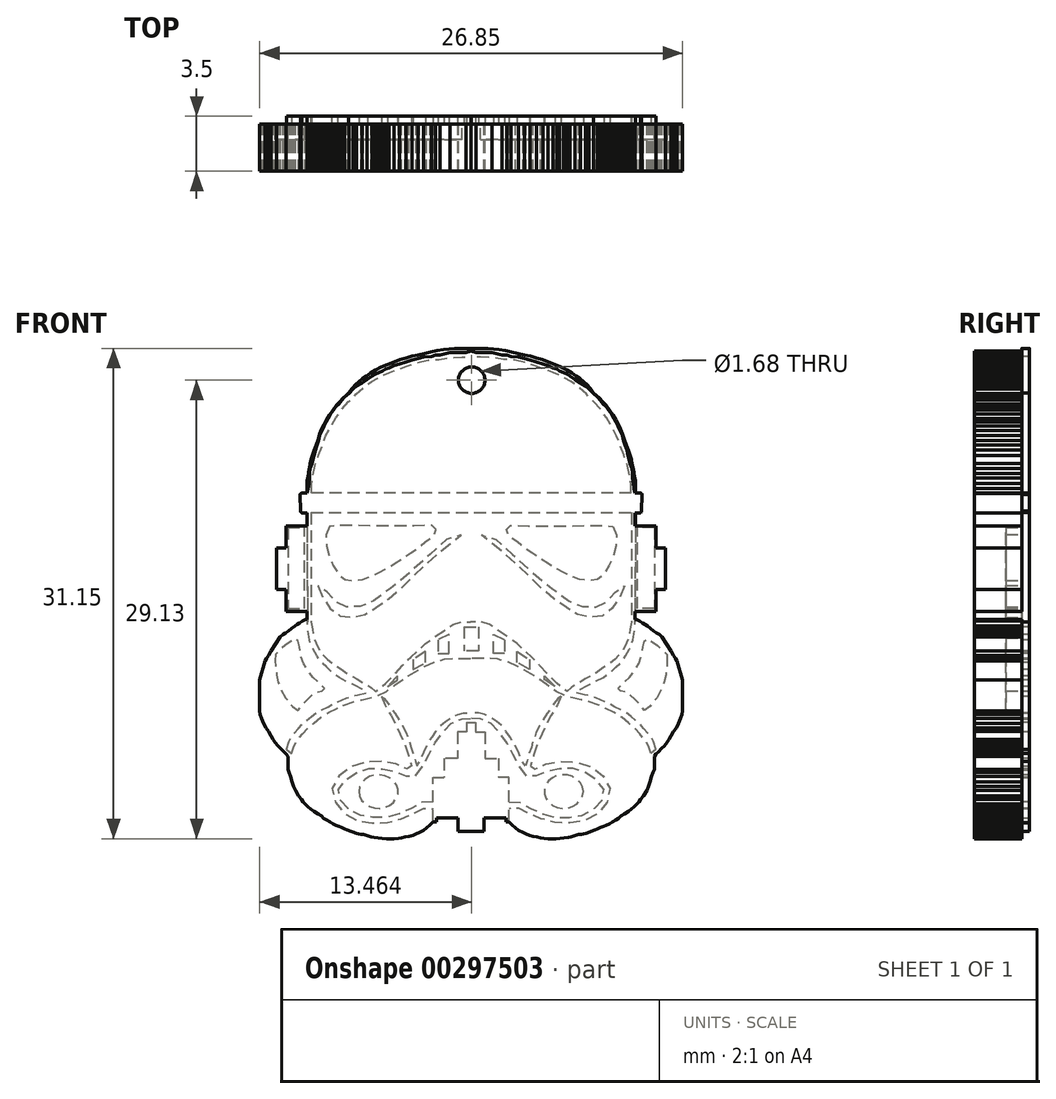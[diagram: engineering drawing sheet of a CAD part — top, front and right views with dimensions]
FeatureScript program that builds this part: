
annotation { "Feature Type Name" : "Feature", "Feature Type Description" : "" }
export const myFeature = defineFeature(function(context is Context, id is Id, definition is map)
    precondition{}
    {
        {
            var Q0;
            Q0=qCreatedBy(makeId("Front.planeOp"),FACE);
            var sketch = newSketch(context, id + "F0", { "sketchPlane" : qUnion([Q0])});
            skLineSegment(sketch, "E0", {"start": v(-15.39, -14.48) * mm, "end": v(-15.53, -14.36) * mm});
            skLineSegment(sketch, "E1", {"start": v(-15.53, -14.36) * mm, "end": v(-15.74, -14.15) * mm});
            skLineSegment(sketch, "E2", {"start": v(-15.74, -14.15) * mm, "end": v(-15.92, -13.98) * mm});
            skLineSegment(sketch, "E3", {"start": v(-15.92, -13.98) * mm, "end": v(-16.08, -13.76) * mm});
            skLineSegment(sketch, "E4", {"start": v(-16.08, -13.76) * mm, "end": v(-16.22, -13.57) * mm});
            skLineSegment(sketch, "E5", {"start": v(-16.22, -13.57) * mm, "end": v(-16.35, -13.35) * mm});
            skLineSegment(sketch, "E6", {"start": v(-16.35, -13.35) * mm, "end": v(-16.5, -13.07) * mm});
            skLineSegment(sketch, "E7", {"start": v(-16.5, -13.07) * mm, "end": v(-16.68, -12.84) * mm});
            skLineSegment(sketch, "E8", {"start": v(-16.68, -12.84) * mm, "end": v(-16.81, -12.57) * mm});
            skLineSegment(sketch, "E9", {"start": v(-16.81, -12.57) * mm, "end": v(-16.95, -12.25) * mm});
            skLineSegment(sketch, "E10", {"start": v(-16.95, -12.25) * mm, "end": v(-17.04, -12) * mm});
            skLineSegment(sketch, "E11", {"start": v(-17.04, -12) * mm, "end": v(-17.07, -11.77) * mm});
            skLineSegment(sketch, "E12", {"start": v(-17.07, -11.77) * mm, "end": v(-17.07, -11.5) * mm});
            skLineSegment(sketch, "E13", {"start": v(-17.07, -11.5) * mm, "end": v(-17.07, -11.27) * mm});
            skLineSegment(sketch, "E14", {"start": v(-17.07, -11.27) * mm, "end": v(-17.07, -10.11) * mm});
            skLineSegment(sketch, "E15", {"start": v(-17.07, -10.11) * mm, "end": v(-17.07, -9.78) * mm});
            skPoint(sketch, "E15.endSnap0", {"position": v(-17.07, -10.7) * mm});
            skLineSegment(sketch, "E16", {"start": v(-17.07, -9.78) * mm, "end": v(-16.99, -9.5) * mm});
            skLineSegment(sketch, "E17", {"start": v(-16.99, -9.5) * mm, "end": v(-16.91, -9.23) * mm});
            skLineSegment(sketch, "E18", {"start": v(-16.91, -9.23) * mm, "end": v(-16.85, -9) * mm});
            skLineSegment(sketch, "E19", {"start": v(-16.85, -9) * mm, "end": v(-16.79, -8.79) * mm});
            skLineSegment(sketch, "E20", {"start": v(-16.79, -8.79) * mm, "end": v(-16.73, -8.58) * mm});
            skLineSegment(sketch, "E21", {"start": v(-16.73, -8.58) * mm, "end": v(-16.63, -8.42) * mm});
            skLineSegment(sketch, "E22", {"start": v(-16.63, -8.42) * mm, "end": v(-16.5, -8.23) * mm});
            skLineSegment(sketch, "E23", {"start": v(-16.5, -8.23) * mm, "end": v(-16.35, -7.95) * mm});
            skLineSegment(sketch, "E24", {"start": v(-16.35, -7.95) * mm, "end": v(-16.14, -7.63) * mm});
            skLineSegment(sketch, "E25", {"start": v(-16.14, -7.63) * mm, "end": v(-15.92, -7.29) * mm});
            skLineSegment(sketch, "E26", {"start": v(-15.92, -7.29) * mm, "end": v(-15.77, -7.05) * mm});
            skLineSegment(sketch, "E27", {"start": v(-15.77, -7.05) * mm, "end": v(-15.6, -6.9) * mm});
            skLineSegment(sketch, "E28", {"start": v(-15.6, -6.9) * mm, "end": v(-15.43, -6.81) * mm});
            skLineSegment(sketch, "E29", {"start": v(-15.43, -6.81) * mm, "end": v(-15.23, -6.67) * mm});
            skLineSegment(sketch, "E30", {"start": v(-15.23, -6.67) * mm, "end": v(-15.04, -6.53) * mm});
            skLineSegment(sketch, "E31", {"start": v(-15.04, -6.53) * mm, "end": v(-14.84, -6.38) * mm});
            skLineSegment(sketch, "E32", {"start": v(-14.84, -6.38) * mm, "end": v(-14.7, -6.28) * mm});
            skLineSegment(sketch, "E33", {"start": v(-14.7, -6.28) * mm, "end": v(-14.54, -6.18) * mm});
            skLineSegment(sketch, "E34", {"start": v(-14.54, -6.18) * mm, "end": v(-14.34, -6.05) * mm});
            skLineSegment(sketch, "E35", {"start": v(-14.34, -6.05) * mm, "end": v(-14.15, -5.96) * mm});
            skLineSegment(sketch, "E36", {"start": v(-14.15, -5.96) * mm, "end": v(-14.06, -5.96) * mm});
            skLineSegment(sketch, "E37", {"start": v(-14.15, 0.83) * mm, "end": v(-14.36, 0.82) * mm});
            skLineSegment(sketch, "E38", {"start": v(-14.48, 0.94) * mm, "end": v(-14.5, 2) * mm});
            skArc(sketch, "E39", {"start": v(-14.48, 0.94) * mm, "mid": v(-14.45, 0.86) * mm, "end": v(-14.36, 0.82) * mm});
            skLineSegment(sketch, "E40", {"start": v(-15.39, -14.48) * mm, "end": v(-15.28, -14.64) * mm});
            skLineSegment(sketch, "E41", {"start": v(-15.28, -14.64) * mm, "end": v(-15.28, -15.48) * mm});
            skLineSegment(sketch, "E42", {"start": v(-15.28, -15.48) * mm, "end": v(-15.2, -15.66) * mm});
            skLineSegment(sketch, "E43", {"start": v(-15.2, -15.66) * mm, "end": v(-15.11, -15.93) * mm});
            skLineSegment(sketch, "E44", {"start": v(-15.11, -15.93) * mm, "end": v(-15, -16.28) * mm});
            skLineSegment(sketch, "E45", {"start": v(-15, -16.28) * mm, "end": v(-14.92, -16.54) * mm});
            skLineSegment(sketch, "E46", {"start": v(-14.92, -16.54) * mm, "end": v(-14.8, -16.82) * mm});
            skLineSegment(sketch, "E47", {"start": v(-14.8, -16.82) * mm, "end": v(-14.6, -17.14) * mm});
            skLineSegment(sketch, "E48", {"start": v(-14.6, -17.14) * mm, "end": v(-14.42, -17.39) * mm});
            skLineSegment(sketch, "E49", {"start": v(-14.42, -17.39) * mm, "end": v(-14.3, -17.52) * mm});
            skLineSegment(sketch, "E50", {"start": v(-14.3, -17.52) * mm, "end": v(-14.18, -17.68) * mm});
            skLineSegment(sketch, "E51", {"start": v(-14.18, -17.68) * mm, "end": v(-14, -17.86) * mm});
            skLineSegment(sketch, "E52", {"start": v(-14, -17.86) * mm, "end": v(-13.84, -18) * mm});
            skLineSegment(sketch, "E53", {"start": v(-13.84, -18) * mm, "end": v(-13.63, -18.15) * mm});
            skLineSegment(sketch, "E54", {"start": v(-13.63, -18.15) * mm, "end": v(-13.38, -18.3) * mm});
            skLineSegment(sketch, "E55", {"start": v(-13.38, -18.3) * mm, "end": v(-13.16, -18.44) * mm});
            skLineSegment(sketch, "E56", {"start": v(-13.16, -18.44) * mm, "end": v(-13, -18.57) * mm});
            skLineSegment(sketch, "E57", {"start": v(-13, -18.57) * mm, "end": v(-12.84, -18.67) * mm});
            skLineSegment(sketch, "E58", {"start": v(-12.84, -18.67) * mm, "end": v(-12.61, -18.81) * mm});
            skLineSegment(sketch, "E59", {"start": v(-12.61, -18.81) * mm, "end": v(-12.42, -18.93) * mm});
            skLineSegment(sketch, "E60", {"start": v(-12.42, -18.93) * mm, "end": v(-12.23, -19.02) * mm});
            skLineSegment(sketch, "E61", {"start": v(-12.23, -19.02) * mm, "end": v(-12.04, -19.09) * mm});
            skLineSegment(sketch, "E62", {"start": v(-12.04, -19.09) * mm, "end": v(-11.86, -19.16) * mm});
            skLineSegment(sketch, "E63", {"start": v(-11.86, -19.16) * mm, "end": v(-11.69, -19.24) * mm});
            skLineSegment(sketch, "E64", {"start": v(-11.69, -19.24) * mm, "end": v(-11.51, -19.31) * mm});
            skLineSegment(sketch, "E65", {"start": v(-11.51, -19.31) * mm, "end": v(-11.34, -19.38) * mm});
            skLineSegment(sketch, "E66", {"start": v(-11.34, -19.38) * mm, "end": v(-11.14, -19.46) * mm});
            skLineSegment(sketch, "E67", {"start": v(-11.14, -19.46) * mm, "end": v(-10.94, -19.53) * mm});
            skLineSegment(sketch, "E68", {"start": v(-10.94, -19.53) * mm, "end": v(-10.8, -19.56) * mm});
            skLineSegment(sketch, "E69", {"start": v(-10.8, -19.56) * mm, "end": v(-10.65, -19.59) * mm});
            skLineSegment(sketch, "E70", {"start": v(-10.65, -19.59) * mm, "end": v(-10.46, -19.59) * mm});
            skLineSegment(sketch, "E71", {"start": v(-10.46, -19.59) * mm, "end": v(-10.23, -19.68) * mm});
            skLineSegment(sketch, "E72", {"start": v(-10.23, -19.68) * mm, "end": v(-10, -19.76) * mm});
            skLineSegment(sketch, "E73", {"start": v(-10, -19.76) * mm, "end": v(-9.82, -19.79) * mm});
            skLineSegment(sketch, "E74", {"start": v(-9.82, -19.79) * mm, "end": v(-9.55, -19.82) * mm});
            skLineSegment(sketch, "E75", {"start": v(-9.55, -19.82) * mm, "end": v(-9.3, -19.85) * mm});
            skLineSegment(sketch, "E76", {"start": v(-9.3, -19.85) * mm, "end": v(-9.03, -19.88) * mm});
            skLineSegment(sketch, "E77", {"start": v(-9.03, -19.88) * mm, "end": v(-8.8, -19.88) * mm});
            skLineSegment(sketch, "E78", {"start": v(-8.8, -19.88) * mm, "end": v(-8.53, -19.88) * mm});
            skLineSegment(sketch, "E79", {"start": v(-8.53, -19.88) * mm, "end": v(-8.26, -19.85) * mm});
            skLineSegment(sketch, "E80", {"start": v(-8.26, -19.85) * mm, "end": v(-8.05, -19.82) * mm});
            skLineSegment(sketch, "E81", {"start": v(-8.05, -19.82) * mm, "end": v(-7.84, -19.76) * mm});
            skLineSegment(sketch, "E82", {"start": v(-7.84, -19.76) * mm, "end": v(-7.58, -19.73) * mm});
            skLineSegment(sketch, "E83", {"start": v(-7.58, -19.73) * mm, "end": v(-7.34, -19.66) * mm});
            skLineSegment(sketch, "E84", {"start": v(-7.34, -19.66) * mm, "end": v(-7.15, -19.56) * mm});
            skLineSegment(sketch, "E85", {"start": v(-7.15, -19.56) * mm, "end": v(-6.93, -19.49) * mm});
            skLineSegment(sketch, "E86", {"start": v(-6.93, -19.49) * mm, "end": v(-6.67, -19.34) * mm});
            skLineSegment(sketch, "E87", {"start": v(-6.67, -19.34) * mm, "end": v(-6.46, -19.2) * mm});
            skLineSegment(sketch, "E88", {"start": v(-6.46, -19.2) * mm, "end": v(-6.25, -19) * mm});
            skLineSegment(sketch, "E89", {"start": v(-6.25, -19) * mm, "end": v(-6.05, -18.8) * mm});
            skLineSegment(sketch, "E90", {"start": v(-6.05, -18.8) * mm, "end": v(-5.85, -18.8) * mm});
            skLineSegment(sketch, "E91", {"start": v(-5.85, -18.8) * mm, "end": v(-5.85, -18.55) * mm});
            skLineSegment(sketch, "E92", {"start": v(-5.85, -18.55) * mm, "end": v(-4.46, -18.55) * mm});
            skLineSegment(sketch, "E93", {"start": v(-4.46, -18.55) * mm, "end": v(-4.46, -19.42) * mm});
            skLineSegment(sketch, "E94", {"start": v(-4.46, -19.42) * mm, "end": v(-3.65, -19.42) * mm});
            skLineSegment(sketch, "E95", {"start": v(-15.39, -14.48) * mm, "end": v(-15.3, -14.37) * mm});
            skLineSegment(sketch, "E96", {"start": v(-15.3, -14.37) * mm, "end": v(-15.22, -14.2) * mm});
            skLineSegment(sketch, "E97", {"start": v(-15.22, -14.2) * mm, "end": v(-15.15, -14.06) * mm});
            skLineSegment(sketch, "E98", {"start": v(-15.15, -14.06) * mm, "end": v(-15.06, -13.9) * mm});
            skLineSegment(sketch, "E99", {"start": v(-15.06, -13.9) * mm, "end": v(-14.98, -13.75) * mm});
            skLineSegment(sketch, "E100", {"start": v(-14.98, -13.75) * mm, "end": v(-14.9, -13.6) * mm});
            skLineSegment(sketch, "E101", {"start": v(-14.9, -13.6) * mm, "end": v(-14.78, -13.45) * mm});
            skLineSegment(sketch, "E102", {"start": v(-14.78, -13.45) * mm, "end": v(-14.68, -13.34) * mm});
            skLineSegment(sketch, "E103", {"start": v(-14.68, -13.34) * mm, "end": v(-14.57, -13.2) * mm});
            skLineSegment(sketch, "E104", {"start": v(-14.57, -13.2) * mm, "end": v(-14.47, -13.07) * mm});
            skLineSegment(sketch, "E105", {"start": v(-14.47, -13.07) * mm, "end": v(-14.34, -12.91) * mm});
            skLineSegment(sketch, "E106", {"start": v(-14.34, -12.91) * mm, "end": v(-14.2, -12.76) * mm});
            skLineSegment(sketch, "E107", {"start": v(-14.2, -12.76) * mm, "end": v(-14.01, -12.63) * mm});
            skLineSegment(sketch, "E108", {"start": v(-14.01, -12.63) * mm, "end": v(-13.9, -12.49) * mm});
            skLineSegment(sketch, "E109", {"start": v(-13.9, -12.49) * mm, "end": v(-13.73, -12.38) * mm});
            skLineSegment(sketch, "E110", {"start": v(-13.73, -12.38) * mm, "end": v(-13.61, -12.24) * mm});
            skLineSegment(sketch, "E111", {"start": v(-13.61, -12.24) * mm, "end": v(-13.45, -12.13) * mm});
            skLineSegment(sketch, "E112", {"start": v(-13.45, -12.13) * mm, "end": v(-13.31, -12.04) * mm});
            skLineSegment(sketch, "E113", {"start": v(-13.31, -12.04) * mm, "end": v(-13.13, -11.92) * mm});
            skLineSegment(sketch, "E114", {"start": v(-13.13, -11.92) * mm, "end": v(-12.98, -11.82) * mm});
            skLineSegment(sketch, "E115", {"start": v(-12.98, -11.82) * mm, "end": v(-12.75, -11.75) * mm});
            skLineSegment(sketch, "E116", {"start": v(-12.75, -11.75) * mm, "end": v(-12.6, -11.64) * mm});
            skLineSegment(sketch, "E117", {"start": v(-12.6, -11.64) * mm, "end": v(-12.45, -11.55) * mm});
            skLineSegment(sketch, "E118", {"start": v(-12.45, -11.55) * mm, "end": v(-12.25, -11.48) * mm});
            skLineSegment(sketch, "E119", {"start": v(-12.25, -11.48) * mm, "end": v(-12.2, -11.44) * mm});
            skLineSegment(sketch, "E120", {"start": v(-12.2, -11.44) * mm, "end": v(-12.03, -11.33) * mm});
            skLineSegment(sketch, "E121", {"start": v(-12.03, -11.33) * mm, "end": v(-11.84, -11.2) * mm});
            skLineSegment(sketch, "E122", {"start": v(-11.84, -11.2) * mm, "end": v(-11.67, -11.16) * mm});
            skLineSegment(sketch, "E123", {"start": v(-11.67, -11.16) * mm, "end": v(-11.46, -11.07) * mm});
            skLineSegment(sketch, "E124", {"start": v(-11.46, -11.07) * mm, "end": v(-11.28, -11.02) * mm});
            skLineSegment(sketch, "E125", {"start": v(-11.28, -11.02) * mm, "end": v(-11.04, -10.95) * mm});
            skLineSegment(sketch, "E126", {"start": v(-11.04, -10.95) * mm, "end": v(-10.67, -10.86) * mm});
            skLineSegment(sketch, "E127", {"start": v(-10.67, -10.86) * mm, "end": v(-10.4, -10.76) * mm});
            skLineSegment(sketch, "E128", {"start": v(-10.4, -10.76) * mm, "end": v(-10.25, -10.7) * mm});
            skLineSegment(sketch, "E129", {"start": v(-10.25, -10.7) * mm, "end": v(-9.95, -10.62) * mm});
            skLineSegment(sketch, "E130", {"start": v(-9.95, -10.62) * mm, "end": v(-9.83, -10.55) * mm});
            skLineSegment(sketch, "E131", {"start": v(-3.65, -19.42) * mm, "end": v(-3.65, 11.1) * mm});
            skLineSegment(sketch, "E132", {"start": v(-3.65, 11.1) * mm, "end": v(-3.97, 11) * mm});
            skLineSegment(sketch, "E133", {"start": v(-3.97, 11) * mm, "end": v(-4.43, 11) * mm});
            skLineSegment(sketch, "E134", {"start": v(-4.43, 11) * mm, "end": v(-4.98, 11) * mm});
            skLineSegment(sketch, "E135", {"start": v(-4.98, 11) * mm, "end": v(-5.6, 10.85) * mm});
            skLineSegment(sketch, "E136", {"start": v(-5.6, 10.85) * mm, "end": v(-5.91, 10.85) * mm});
            skLineSegment(sketch, "E137", {"start": v(-5.91, 10.85) * mm, "end": v(-6.17, 10.76) * mm});
            skLineSegment(sketch, "E138", {"start": v(-6.17, 10.76) * mm, "end": v(-6.66, 10.72) * mm});
            skLineSegment(sketch, "E139", {"start": v(-6.66, 10.72) * mm, "end": v(-7.03, 10.63) * mm});
            skLineSegment(sketch, "E140", {"start": v(-7.03, 10.63) * mm, "end": v(-7.4, 10.53) * mm});
            skLineSegment(sketch, "E141", {"start": v(-7.4, 10.53) * mm, "end": v(-7.78, 10.4) * mm});
            skLineSegment(sketch, "E142", {"start": v(-7.78, 10.4) * mm, "end": v(-8.2, 10.28) * mm});
            skLineSegment(sketch, "E143", {"start": v(-8.2, 10.28) * mm, "end": v(-8.53, 10.17) * mm});
            skLineSegment(sketch, "E144", {"start": v(-8.53, 10.17) * mm, "end": v(-8.85, 10.03) * mm});
            skLineSegment(sketch, "E145", {"start": v(-8.85, 10.03) * mm, "end": v(-9.1, 9.94) * mm});
            skLineSegment(sketch, "E146", {"start": v(-9.1, 9.94) * mm, "end": v(-9.27, 9.83) * mm});
            skLineSegment(sketch, "E147", {"start": v(-9.27, 9.83) * mm, "end": v(-9.5, 9.73) * mm});
            skLineSegment(sketch, "E148", {"start": v(-9.5, 9.73) * mm, "end": v(-9.72, 9.63) * mm});
            skLineSegment(sketch, "E149", {"start": v(-9.72, 9.63) * mm, "end": v(-9.93, 9.51) * mm});
            skLineSegment(sketch, "E150", {"start": v(-9.93, 9.51) * mm, "end": v(-10.24, 9.3) * mm});
            skLineSegment(sketch, "E151", {"start": v(-10.24, 9.3) * mm, "end": v(-10.58, 9.07) * mm});
            skLineSegment(sketch, "E152", {"start": v(-10.58, 9.07) * mm, "end": v(-10.91, 8.86) * mm});
            skLineSegment(sketch, "E153", {"start": v(-10.91, 8.86) * mm, "end": v(-11.14, 8.68) * mm});
            skLineSegment(sketch, "E154", {"start": v(-11.14, 8.68) * mm, "end": v(-11.41, 8.42) * mm});
            skLineSegment(sketch, "E155", {"start": v(-11.41, 8.42) * mm, "end": v(-11.67, 8.17) * mm});
            skLineSegment(sketch, "E156", {"start": v(-11.67, 8.17) * mm, "end": v(-11.83, 7.98) * mm});
            skLineSegment(sketch, "E157", {"start": v(-11.83, 7.98) * mm, "end": v(-12.03, 7.75) * mm});
            skLineSegment(sketch, "E158", {"start": v(-12.03, 7.75) * mm, "end": v(-12.25, 7.53) * mm});
            skLineSegment(sketch, "E159", {"start": v(-12.25, 7.53) * mm, "end": v(-12.39, 7.35) * mm});
            skLineSegment(sketch, "E160", {"start": v(-12.39, 7.35) * mm, "end": v(-12.56, 7.09) * mm});
            skLineSegment(sketch, "E161", {"start": v(-12.56, 7.09) * mm, "end": v(-12.72, 6.82) * mm});
            skLineSegment(sketch, "E162", {"start": v(-12.72, 6.82) * mm, "end": v(-12.84, 6.59) * mm});
            skLineSegment(sketch, "E163", {"start": v(-12.84, 6.59) * mm, "end": v(-12.99, 6.33) * mm});
            skLineSegment(sketch, "E164", {"start": v(-12.99, 6.33) * mm, "end": v(-13.1, 6.07) * mm});
            skLineSegment(sketch, "E165", {"start": v(-13.1, 6.07) * mm, "end": v(-13.26, 5.74) * mm});
            skLineSegment(sketch, "E166", {"start": v(-13.26, 5.74) * mm, "end": v(-13.33, 5.41) * mm});
            skLineSegment(sketch, "E167", {"start": v(-13.33, 5.41) * mm, "end": v(-13.42, 5.13) * mm});
            skLineSegment(sketch, "E168", {"start": v(-13.42, 5.13) * mm, "end": v(-13.53, 4.8) * mm});
            skLineSegment(sketch, "E169", {"start": v(-13.53, 4.8) * mm, "end": v(-13.6, 4.46) * mm});
            skLineSegment(sketch, "E170", {"start": v(-13.6, 4.46) * mm, "end": v(-13.67, 4.2) * mm});
            skLineSegment(sketch, "E171", {"start": v(-13.67, 4.2) * mm, "end": v(-13.74, 3.94) * mm});
            skLineSegment(sketch, "E172", {"start": v(-13.74, 3.94) * mm, "end": v(-13.86, 3.64) * mm});
            skLineSegment(sketch, "E173", {"start": v(-14, 2.36) * mm, "end": v(-13.95, 2.68) * mm});
            skLineSegment(sketch, "E174", {"start": v(-13.95, 2.68) * mm, "end": v(-13.9, 3.04) * mm});
            skLineSegment(sketch, "E175", {"start": v(-13.9, 3.04) * mm, "end": v(-13.9, 3.3) * mm});
            skLineSegment(sketch, "E176", {"start": v(-13.9, 3.3) * mm, "end": v(-13.86, 3.64) * mm});
            skLineSegment(sketch, "E177", {"start": v(-14.06, -5.96) * mm, "end": v(-14.06, 0.83) * mm});
            skLineSegment(sketch, "E178", {"start": v(-14.06, 0.83) * mm, "end": v(-14.15, 0.83) * mm});
            skArc(sketch, "E179", {"start": v(-14.43, 2.06) * mm, "mid": v(-14.48, 2.05) * mm, "end": v(-14.5, 2) * mm});
            skPoint(sketch, "E180.end.orphan", {"position": v(-14.06, 2.07) * mm});
            skLineSegment(sketch, "E181", {"start": v(-14.44, 2.06) * mm, "end": v(-14.06, 2.07) * mm});
            skLineSegment(sketch, "E182", {"start": v(-14.06, 2.07) * mm, "end": v(-14.03, 2.2) * mm});
            skLineSegment(sketch, "E183", {"start": v(-14.03, 2.2) * mm, "end": v(-14, 2.36) * mm});
            skLineSegment(sketch, "E184", {"start": v(-15.4, 0) * mm, "end": v(-14.06, 0) * mm});
            skLineSegment(sketch, "E185", {"start": v(-15.4, 0) * mm, "end": v(-15.4, -5.45) * mm});
            skLineSegment(sketch, "E186", {"start": v(-15.4, -5.45) * mm, "end": v(-14.06, -5.45) * mm});
            skLineSegment(sketch, "E187", {"start": v(-15.4, -1.4) * mm, "end": v(-16, -1.4) * mm});
            skLineSegment(sketch, "E188", {"start": v(-16, -1.4) * mm, "end": v(-16, -4.06) * mm});
            skLineSegment(sketch, "E189", {"start": v(-16, -4.06) * mm, "end": v(-15.4, -4.06) * mm});
            skLineSegment(sketch, "E190", {"start": v(-3.65, -12.5) * mm, "end": v(-3.93, -12.5) * mm});
            skLineSegment(sketch, "E191", {"start": v(-3.93, -12.5) * mm, "end": v(-3.93, -13.1) * mm});
            skLineSegment(sketch, "E192", {"start": v(-3.93, -13.1) * mm, "end": v(-4.52, -13.1) * mm});
            skLineSegment(sketch, "E193", {"start": v(-4.52, -13.1) * mm, "end": v(-4.52, -14.78) * mm});
            skLineSegment(sketch, "E194", {"start": v(-4.52, -14.78) * mm, "end": v(-5.37, -14.78) * mm});
            skLineSegment(sketch, "E195", {"start": v(-5.37, -14.78) * mm, "end": v(-5.37, -15.97) * mm});
            skLineSegment(sketch, "E196", {"start": v(-6.05, -18.8) * mm, "end": v(-6.05, -16) * mm});
            skLineSegment(sketch, "E197", {"start": v(-6.05, -16) * mm, "end": v(-5.37, -15.97) * mm});
            skLineSegment(sketch, "E198.MirrorCS", {"start": v(6.77, 0.83) * mm, "end": v(6.86, 0.83) * mm});
            skLineSegment(sketch, "E199.MirrorCS", {"start": v(8.1, -14.48) * mm, "end": v(8, -14.37) * mm});
            skLineSegment(sketch, "E200.MirrorCS", {"start": v(2.94, -19.68) * mm, "end": v(2.7, -19.76) * mm});
            skLineSegment(sketch, "E201.MirrorCS", {"start": v(7.93, -14.2) * mm, "end": v(7.86, -14.06) * mm});
            skLineSegment(sketch, "E202.MirrorCS", {"start": v(3.17, -19.59) * mm, "end": v(2.94, -19.68) * mm});
            skLineSegment(sketch, "E203.MirrorCS", {"start": v(3.35, -19.59) * mm, "end": v(3.17, -19.59) * mm});
            skLineSegment(sketch, "E204.MirrorCS", {"start": v(3.5, -19.56) * mm, "end": v(3.35, -19.59) * mm});
            skLineSegment(sketch, "E205.MirrorCS", {"start": v(3.64, -19.53) * mm, "end": v(3.5, -19.56) * mm});
            skLineSegment(sketch, "E206.MirrorCS", {"start": v(3.84, -19.46) * mm, "end": v(3.64, -19.53) * mm});
            skArc(sketch, "E207.MirrorCS", {"start": v(7.14, 2.06) * mm, "mid": v(7.19, 2.05) * mm, "end": v(7.2, 2) * mm});
            skLineSegment(sketch, "E208.MirrorCS", {"start": v(4.74, -11.33) * mm, "end": v(4.55, -11.2) * mm});
            skLineSegment(sketch, "E209.MirrorCS", {"start": v(8.24, -14.36) * mm, "end": v(8.45, -14.15) * mm});
            skLineSegment(sketch, "E210.MirrorCS", {"start": v(8.1, -14.48) * mm, "end": v(7.99, -14.64) * mm});
            skLineSegment(sketch, "E211.MirrorCS", {"start": v(8, -14.37) * mm, "end": v(7.93, -14.2) * mm});
            skLineSegment(sketch, "E212.MirrorCS", {"start": v(0.97, -19.85) * mm, "end": v(0.76, -19.82) * mm});
            skLineSegment(sketch, "E213.MirrorCS", {"start": v(7.75, -6.53) * mm, "end": v(7.55, -6.38) * mm});
            skLineSegment(sketch, "E214.MirrorCS", {"start": v(1.23, -19.88) * mm, "end": v(0.97, -19.85) * mm});
            skLineSegment(sketch, "E215.MirrorCS", {"start": v(4.57, -19.16) * mm, "end": v(4.4, -19.24) * mm});
            skLineSegment(sketch, "E216.MirrorCS", {"start": v(6.6, 3.04) * mm, "end": v(6.6, 3.3) * mm});
            skLineSegment(sketch, "E217.MirrorCS", {"start": v(6.66, 2.68) * mm, "end": v(6.6, 3.04) * mm});
            skLineSegment(sketch, "E218.MirrorCS", {"start": v(1.51, -19.88) * mm, "end": v(1.23, -19.88) * mm});
            skLineSegment(sketch, "E219.MirrorCS", {"start": v(6.71, 2.36) * mm, "end": v(6.66, 2.68) * mm});
            skLineSegment(sketch, "E220.MirrorCS", {"start": v(1.74, -19.88) * mm, "end": v(1.51, -19.88) * mm});
            skLineSegment(sketch, "E221.MirrorCS", {"start": v(2, -19.85) * mm, "end": v(1.74, -19.88) * mm});
            skLineSegment(sketch, "E222.MirrorCS", {"start": v(4.96, -11.48) * mm, "end": v(4.9, -11.44) * mm});
            skArc(sketch, "E223.MirrorCS", {"start": v(7.2, 0.94) * mm, "mid": v(7.15, 0.86) * mm, "end": v(7.07, 0.82) * mm});
            skLineSegment(sketch, "E224.MirrorCS", {"start": v(6.74, 2.2) * mm, "end": v(6.71, 2.36) * mm});
            skLineSegment(sketch, "E225.MirrorCS", {"start": v(6.77, 2.07) * mm, "end": v(6.74, 2.2) * mm});
            skLineSegment(sketch, "E226.MirrorCS", {"start": v(6.86, 0.83) * mm, "end": v(7.07, 0.82) * mm});
            skLineSegment(sketch, "E227.MirrorCS", {"start": v(7.86, -14.06) * mm, "end": v(7.77, -13.9) * mm});
            skLineSegment(sketch, "E228.MirrorCS", {"start": v(7.15, 2.06) * mm, "end": v(6.77, 2.07) * mm});
            skLineSegment(sketch, "E229.MirrorCS", {"start": v(7.7, -13.75) * mm, "end": v(7.61, -13.6) * mm});
            skLineSegment(sketch, "E230.MirrorCS", {"start": v(7.77, -13.9) * mm, "end": v(7.7, -13.75) * mm});
            skLineSegment(sketch, "E231.MirrorCS", {"start": v(8.1, -14.48) * mm, "end": v(8.24, -14.36) * mm});
            skLineSegment(sketch, "E232.MirrorCS", {"start": v(4.17, -11.07) * mm, "end": v(3.99, -11.02) * mm});
            skLineSegment(sketch, "E233.MirrorCS", {"start": v(7.92, -15.66) * mm, "end": v(7.82, -15.93) * mm});
            skLineSegment(sketch, "E234.MirrorCS", {"start": v(7.25, -6.18) * mm, "end": v(7.05, -6.05) * mm});
            skLineSegment(sketch, "E235.MirrorCS", {"start": v(4.04, -19.38) * mm, "end": v(3.84, -19.46) * mm});
            skLineSegment(sketch, "E236.MirrorCS", {"start": v(5.7, -18.57) * mm, "end": v(5.55, -18.67) * mm});
            skLineSegment(sketch, "E237.MirrorCS", {"start": v(5.86, -18.44) * mm, "end": v(5.7, -18.57) * mm});
            skLineSegment(sketch, "E238.MirrorCS", {"start": v(4.9, -11.44) * mm, "end": v(4.74, -11.33) * mm});
            skLineSegment(sketch, "E239.MirrorCS", {"start": v(0.55, -19.76) * mm, "end": v(0.28, -19.73) * mm});
            skLineSegment(sketch, "E240.MirrorCS", {"start": v(4.22, -19.31) * mm, "end": v(4.04, -19.38) * mm});
            skLineSegment(sketch, "E241.MirrorCS", {"start": v(7.4, -6.28) * mm, "end": v(7.25, -6.18) * mm});
            skLineSegment(sketch, "E242.MirrorCS", {"start": v(0.76, -19.82) * mm, "end": v(0.55, -19.76) * mm});
            skLineSegment(sketch, "E243.MirrorCS", {"start": v(6.6, 3.3) * mm, "end": v(6.57, 3.64) * mm});
            skLineSegment(sketch, "E244.MirrorCS", {"start": v(6.16, -12.13) * mm, "end": v(6.02, -12.04) * mm});
            skLineSegment(sketch, "E245.MirrorCS", {"start": v(4.4, -19.24) * mm, "end": v(4.22, -19.31) * mm});
            skLineSegment(sketch, "E246.MirrorCS", {"start": v(7.55, -6.38) * mm, "end": v(7.4, -6.28) * mm});
            skLineSegment(sketch, "E247.MirrorCS", {"start": v(3.38, -10.86) * mm, "end": v(3.12, -10.76) * mm});
            skLineSegment(sketch, "E248.MirrorCS", {"start": v(6.02, -12.04) * mm, "end": v(5.84, -11.92) * mm});
            skLineSegment(sketch, "E249.MirrorCS", {"start": v(6.32, -12.24) * mm, "end": v(6.16, -12.13) * mm});
            skLineSegment(sketch, "E250.MirrorCS", {"start": v(3.75, -10.95) * mm, "end": v(3.38, -10.86) * mm});
            skLineSegment(sketch, "E251.MirrorCS", {"start": v(7.94, -6.67) * mm, "end": v(7.75, -6.53) * mm});
            skLineSegment(sketch, "E252.MirrorCS", {"start": v(4.75, -19.09) * mm, "end": v(4.57, -19.16) * mm});
            skLineSegment(sketch, "E253.MirrorCS", {"start": v(3.99, -11.02) * mm, "end": v(3.75, -10.95) * mm});
            skLineSegment(sketch, "E254.MirrorCS", {"start": v(4.93, -19.02) * mm, "end": v(4.75, -19.09) * mm});
            skLineSegment(sketch, "E255.MirrorCS", {"start": v(8.14, -6.81) * mm, "end": v(7.94, -6.67) * mm});
            skLineSegment(sketch, "E256.MirrorCS", {"start": v(8.3, -6.9) * mm, "end": v(8.14, -6.81) * mm});
            skLineSegment(sketch, "E257.MirrorCS", {"start": v(5.13, -18.93) * mm, "end": v(4.93, -19.02) * mm});
            skLineSegment(sketch, "E258.MirrorCS", {"start": v(7.99, -15.48) * mm, "end": v(7.92, -15.66) * mm});
            skLineSegment(sketch, "E259.MirrorCS", {"start": v(8.63, -7.29) * mm, "end": v(8.48, -7.05) * mm});
            skLineSegment(sketch, "E260.MirrorCS", {"start": v(4.55, -11.2) * mm, "end": v(4.38, -11.16) * mm});
            skLineSegment(sketch, "E261.MirrorCS", {"start": v(5.55, -18.67) * mm, "end": v(5.32, -18.81) * mm});
            skLineSegment(sketch, "E262.MirrorCS", {"start": v(4.38, -11.16) * mm, "end": v(4.17, -11.07) * mm});
            skLineSegment(sketch, "E263.MirrorCS", {"start": v(5.32, -18.81) * mm, "end": v(5.13, -18.93) * mm});
            skLineSegment(sketch, "E264.MirrorCS", {"start": v(8.48, -7.05) * mm, "end": v(8.3, -6.9) * mm});
            skLineSegment(sketch, "E265.MirrorCS", {"start": v(7.99, -14.64) * mm, "end": v(7.99, -15.48) * mm});
            skLineSegment(sketch, "E266.MirrorCS", {"start": v(2.7, -19.76) * mm, "end": v(2.53, -19.79) * mm});
            skLineSegment(sketch, "E267.MirrorCS", {"start": v(7.4, -13.34) * mm, "end": v(7.28, -13.2) * mm});
            skLineSegment(sketch, "E268.MirrorCS", {"start": v(6.09, -18.3) * mm, "end": v(5.86, -18.44) * mm});
            skLineSegment(sketch, "E269.MirrorCS", {"start": v(6.34, -18.15) * mm, "end": v(6.09, -18.3) * mm});
            skLineSegment(sketch, "E270.MirrorCS", {"start": v(7.2, 0.94) * mm, "end": v(7.2, 2) * mm});
            skLineSegment(sketch, "E271.MirrorCS", {"start": v(5.84, -11.92) * mm, "end": v(5.69, -11.82) * mm});
            skLineSegment(sketch, "E272.MirrorCS", {"start": v(-2.86, 11) * mm, "end": v(-2.32, 11) * mm});
            skLineSegment(sketch, "E273.MirrorCS", {"start": v(5.16, -11.55) * mm, "end": v(4.96, -11.48) * mm});
            skLineSegment(sketch, "E274.MirrorCS", {"start": v(7.5, -13.45) * mm, "end": v(7.4, -13.34) * mm});
            skLineSegment(sketch, "E275.MirrorCS", {"start": v(-3.65, 11.1) * mm, "end": v(-3.32, 11) * mm});
            skLineSegment(sketch, "E276.MirrorCS", {"start": v(-3.32, 11) * mm, "end": v(-2.86, 11) * mm});
            skLineSegment(sketch, "E277.MirrorCS", {"start": v(7.61, -13.6) * mm, "end": v(7.5, -13.45) * mm});
            skLineSegment(sketch, "E278.MirrorCS", {"start": v(5.3, -11.64) * mm, "end": v(5.16, -11.55) * mm});
            skLineSegment(sketch, "E279.MirrorCS", {"start": v(5.46, -11.75) * mm, "end": v(5.3, -11.64) * mm});
            skLineSegment(sketch, "E280.MirrorCS", {"start": v(6.86, -5.96) * mm, "end": v(6.77, -5.96) * mm});
            skLineSegment(sketch, "E281.MirrorCS", {"start": v(5.69, -11.82) * mm, "end": v(5.46, -11.75) * mm});
            skLineSegment(sketch, "E282.MirrorCS", {"start": v(0.28, -19.73) * mm, "end": v(0.05, -19.66) * mm});
            skLineSegment(sketch, "E283.MirrorCS", {"start": v(7.05, -6.05) * mm, "end": v(6.86, -5.96) * mm});
            skLineSegment(sketch, "E284.MirrorCS", {"start": v(9.66, -12.25) * mm, "end": v(9.75, -12) * mm});
            skLineSegment(sketch, "E285.MirrorCS", {"start": v(-1.44, -18.8) * mm, "end": v(-1.44, -18.55) * mm});
            skLineSegment(sketch, "E286.MirrorCS", {"start": v(6.38, 4.2) * mm, "end": v(6.45, 3.94) * mm});
            skLineSegment(sketch, "E287.MirrorCS", {"start": v(-1.24, -18.8) * mm, "end": v(-1.44, -18.8) * mm});
            skLineSegment(sketch, "E288.MirrorCS", {"start": v(6.24, 4.8) * mm, "end": v(6.32, 4.46) * mm});
            skLineSegment(sketch, "E289.MirrorCS", {"start": v(-1.04, -19) * mm, "end": v(-1.24, -18.8) * mm});
            skLineSegment(sketch, "E290.MirrorCS", {"start": v(-0.83, -19.2) * mm, "end": v(-1.04, -19) * mm});
            skLineSegment(sketch, "E291.MirrorCS", {"start": v(9.7, -9.5) * mm, "end": v(9.62, -9.23) * mm});
            skLineSegment(sketch, "E292.MirrorCS", {"start": v(9.75, -12) * mm, "end": v(9.78, -11.77) * mm});
            skLineSegment(sketch, "E293.MirrorCS", {"start": v(9.78, -9.78) * mm, "end": v(9.7, -9.5) * mm});
            skLineSegment(sketch, "E294.MirrorCS", {"start": v(9.62, -9.23) * mm, "end": v(9.56, -9) * mm});
            skLineSegment(sketch, "E295.MirrorCS", {"start": v(9.78, -10.11) * mm, "end": v(9.78, -9.78) * mm});
            skLineSegment(sketch, "E296.MirrorCS", {"start": v(9.78, -11.27) * mm, "end": v(9.78, -10.11) * mm});
            skLineSegment(sketch, "E297.MirrorCS", {"start": v(9.78, -11.5) * mm, "end": v(9.78, -11.27) * mm});
            skLineSegment(sketch, "E298.MirrorCS", {"start": v(9.78, -11.77) * mm, "end": v(9.78, -11.5) * mm});
            skLineSegment(sketch, "E299.MirrorCS", {"start": v(7.82, -15.93) * mm, "end": v(7.71, -16.28) * mm});
            skLineSegment(sketch, "E300.MirrorCS", {"start": v(6.32, 4.46) * mm, "end": v(6.38, 4.2) * mm});
            skLineSegment(sketch, "E301.MirrorCS", {"start": v(7.05, -12.91) * mm, "end": v(6.92, -12.76) * mm});
            skLineSegment(sketch, "E302.MirrorCS", {"start": v(2.53, -19.79) * mm, "end": v(2.26, -19.82) * mm});
            skLineSegment(sketch, "E303.MirrorCS", {"start": v(6.45, 3.94) * mm, "end": v(6.57, 3.64) * mm});
            skLineSegment(sketch, "E304.MirrorCS", {"start": v(2.26, -19.82) * mm, "end": v(2, -19.85) * mm});
            skLineSegment(sketch, "E305.MirrorCS", {"start": v(8.84, -7.63) * mm, "end": v(8.63, -7.29) * mm});
            skLineSegment(sketch, "E306.MirrorCS", {"start": v(9.52, -12.57) * mm, "end": v(9.66, -12.25) * mm});
            skLineSegment(sketch, "E307.MirrorCS", {"start": v(8.63, -13.98) * mm, "end": v(8.8, -13.76) * mm});
            skLineSegment(sketch, "E308.MirrorCS", {"start": v(9.44, -8.58) * mm, "end": v(9.34, -8.42) * mm});
            skLineSegment(sketch, "E309.MirrorCS", {"start": v(9.5, -8.79) * mm, "end": v(9.44, -8.58) * mm});
            skLineSegment(sketch, "E310.MirrorCS", {"start": v(9.56, -9) * mm, "end": v(9.5, -8.79) * mm});
            skLineSegment(sketch, "E311.MirrorCS", {"start": v(8.45, -14.15) * mm, "end": v(8.63, -13.98) * mm});
            skLineSegment(sketch, "E312.MirrorCS", {"start": v(6.72, -12.63) * mm, "end": v(6.6, -12.49) * mm});
            skLineSegment(sketch, "E313.MirrorCS", {"start": v(-0.26, 10.63) * mm, "end": v(0.1, 10.53) * mm});
            skLineSegment(sketch, "E314.MirrorCS", {"start": v(6.92, -12.76) * mm, "end": v(6.72, -12.63) * mm});
            skLineSegment(sketch, "E315.MirrorCS", {"start": v(8.1, -1.4) * mm, "end": v(8.7, -1.4) * mm});
            skLineSegment(sketch, "E316.MirrorCS", {"start": v(-1.12, 10.76) * mm, "end": v(-0.63, 10.72) * mm});
            skLineSegment(sketch, "E317.MirrorCS", {"start": v(3.62, 8.86) * mm, "end": v(3.85, 8.68) * mm});
            skLineSegment(sketch, "E318.MirrorCS", {"start": v(7.18, -13.07) * mm, "end": v(7.05, -12.91) * mm});
            skLineSegment(sketch, "E319.MirrorCS", {"start": v(-1.38, 10.85) * mm, "end": v(-1.12, 10.76) * mm});
            skLineSegment(sketch, "E320.MirrorCS", {"start": v(5.26, 7.09) * mm, "end": v(5.43, 6.82) * mm});
            skLineSegment(sketch, "E321.MirrorCS", {"start": v(9.39, -12.84) * mm, "end": v(9.52, -12.57) * mm});
            skLineSegment(sketch, "E322.MirrorCS", {"start": v(9.06, -7.95) * mm, "end": v(8.84, -7.63) * mm});
            skLineSegment(sketch, "E323.MirrorCS", {"start": v(7.28, -13.2) * mm, "end": v(7.18, -13.07) * mm});
            skLineSegment(sketch, "E324.MirrorCS", {"start": v(7.13, -17.39) * mm, "end": v(7.01, -17.52) * mm});
            skLineSegment(sketch, "E325.MirrorCS", {"start": v(3.29, 9.07) * mm, "end": v(3.62, 8.86) * mm});
            skLineSegment(sketch, "E326.MirrorCS", {"start": v(7.01, -17.52) * mm, "end": v(6.89, -17.68) * mm});
            skLineSegment(sketch, "E327.MirrorCS", {"start": v(5.1, 7.35) * mm, "end": v(5.26, 7.09) * mm});
            skLineSegment(sketch, "E328.MirrorCS", {"start": v(3.12, -10.76) * mm, "end": v(2.96, -10.7) * mm});
            skLineSegment(sketch, "E329.MirrorCS", {"start": v(7.32, -17.14) * mm, "end": v(7.13, -17.39) * mm});
            skLineSegment(sketch, "E330.MirrorCS", {"start": v(1.24, 10.17) * mm, "end": v(1.56, 10.03) * mm});
            skLineSegment(sketch, "E331.MirrorCS", {"start": v(7.52, -16.82) * mm, "end": v(7.32, -17.14) * mm});
            skLineSegment(sketch, "E332.MirrorCS", {"start": v(0.9, 10.28) * mm, "end": v(1.24, 10.17) * mm});
            skLineSegment(sketch, "E333.MirrorCS", {"start": v(-2.32, 11) * mm, "end": v(-1.69, 10.85) * mm});
            skLineSegment(sketch, "E334.MirrorCS", {"start": v(-3.36, -13.1) * mm, "end": v(-2.77, -13.1) * mm});
            skLineSegment(sketch, "E335.MirrorCS", {"start": v(5.43, 6.82) * mm, "end": v(5.55, 6.59) * mm});
            skLineSegment(sketch, "E336.MirrorCS", {"start": v(4.96, 7.53) * mm, "end": v(5.1, 7.35) * mm});
            skLineSegment(sketch, "E337.MirrorCS", {"start": v(2.66, -10.62) * mm, "end": v(2.54, -10.55) * mm});
            skLineSegment(sketch, "E338.MirrorCS", {"start": v(4.74, 7.75) * mm, "end": v(4.96, 7.53) * mm});
            skLineSegment(sketch, "E339.MirrorCS", {"start": v(6.44, -12.38) * mm, "end": v(6.32, -12.24) * mm});
            skLineSegment(sketch, "E340.MirrorCS", {"start": v(-2.83, -19.42) * mm, "end": v(-3.65, -19.42) * mm});
            skLineSegment(sketch, "E341.MirrorCS", {"start": v(-3.36, -12.5) * mm, "end": v(-3.36, -13.1) * mm});
            skLineSegment(sketch, "E342.MirrorCS", {"start": v(0.5, 10.4) * mm, "end": v(0.9, 10.28) * mm});
            skLineSegment(sketch, "E343.MirrorCS", {"start": v(7.63, -16.54) * mm, "end": v(7.52, -16.82) * mm});
            skLineSegment(sketch, "E344.MirrorCS", {"start": v(6.6, -12.49) * mm, "end": v(6.44, -12.38) * mm});
            skLineSegment(sketch, "E345.MirrorCS", {"start": v(-2.83, -18.55) * mm, "end": v(-2.83, -19.42) * mm});
            skLineSegment(sketch, "E346.MirrorCS", {"start": v(7.71, -16.28) * mm, "end": v(7.63, -16.54) * mm});
            skLineSegment(sketch, "E347.MirrorCS", {"start": v(0.1, 10.53) * mm, "end": v(0.5, 10.4) * mm});
            skLineSegment(sketch, "E348.MirrorCS", {"start": v(-3.65, -12.5) * mm, "end": v(-3.36, -12.5) * mm});
            skLineSegment(sketch, "E349.MirrorCS", {"start": v(4.54, 7.98) * mm, "end": v(4.74, 7.75) * mm});
            skLineSegment(sketch, "E350.MirrorCS", {"start": v(4.38, 8.17) * mm, "end": v(4.54, 7.98) * mm});
            skLineSegment(sketch, "E351.MirrorCS", {"start": v(3.85, 8.68) * mm, "end": v(4.12, 8.42) * mm});
            skLineSegment(sketch, "E352.MirrorCS", {"start": v(-1.44, -18.55) * mm, "end": v(-2.83, -18.55) * mm});
            skLineSegment(sketch, "E353.MirrorCS", {"start": v(8.7, -4.06) * mm, "end": v(8.1, -4.06) * mm});
            skLineSegment(sketch, "E354.MirrorCS", {"start": v(-0.63, 10.72) * mm, "end": v(-0.26, 10.63) * mm});
            skLineSegment(sketch, "E355.MirrorCS", {"start": v(4.12, 8.42) * mm, "end": v(4.38, 8.17) * mm});
            skLineSegment(sketch, "E356.MirrorCS", {"start": v(6.04, 5.41) * mm, "end": v(6.12, 5.13) * mm});
            skLineSegment(sketch, "E357.MirrorCS", {"start": v(2.95, 9.3) * mm, "end": v(3.29, 9.07) * mm});
            skLineSegment(sketch, "E358.MirrorCS", {"start": v(9.22, -8.23) * mm, "end": v(9.06, -7.95) * mm});
            skLineSegment(sketch, "E359.MirrorCS", {"start": v(-0.62, -19.34) * mm, "end": v(-0.83, -19.2) * mm});
            skLineSegment(sketch, "E360.MirrorCS", {"start": v(-1.69, 10.85) * mm, "end": v(-1.38, 10.85) * mm});
            skLineSegment(sketch, "E361.MirrorCS", {"start": v(8.93, -13.57) * mm, "end": v(9.06, -13.35) * mm});
            skLineSegment(sketch, "E362.MirrorCS", {"start": v(-2.77, -14.78) * mm, "end": v(-1.92, -14.78) * mm});
            skLineSegment(sketch, "E363.MirrorCS", {"start": v(2.96, -10.7) * mm, "end": v(2.66, -10.62) * mm});
            skLineSegment(sketch, "E364.MirrorCS", {"start": v(9.34, -8.42) * mm, "end": v(9.22, -8.23) * mm});
            skLineSegment(sketch, "E365.MirrorCS", {"start": v(8.8, -13.76) * mm, "end": v(8.93, -13.57) * mm});
            skLineSegment(sketch, "E366.MirrorCS", {"start": v(6.12, 5.13) * mm, "end": v(6.24, 4.8) * mm});
            skLineSegment(sketch, "E367.MirrorCS", {"start": v(5.97, 5.74) * mm, "end": v(6.04, 5.41) * mm});
            skLineSegment(sketch, "E368.MirrorCS", {"start": v(2.63, 9.51) * mm, "end": v(2.95, 9.3) * mm});
            skLineSegment(sketch, "E369.MirrorCS", {"start": v(-0.36, -19.49) * mm, "end": v(-0.62, -19.34) * mm});
            skLineSegment(sketch, "E370.MirrorCS", {"start": v(1.56, 10.03) * mm, "end": v(1.8, 9.94) * mm});
            skLineSegment(sketch, "E371.MirrorCS", {"start": v(-1.24, -16) * mm, "end": v(-1.92, -15.97) * mm});
            skLineSegment(sketch, "E372.MirrorCS", {"start": v(1.8, 9.94) * mm, "end": v(1.98, 9.83) * mm});
            skLineSegment(sketch, "E373.MirrorCS", {"start": v(2.21, 9.73) * mm, "end": v(2.43, 9.63) * mm});
            skLineSegment(sketch, "E374.MirrorCS", {"start": v(2.43, 9.63) * mm, "end": v(2.63, 9.51) * mm});
            skLineSegment(sketch, "E375.MirrorCS", {"start": v(-0.14, -19.56) * mm, "end": v(-0.36, -19.49) * mm});
            skLineSegment(sketch, "E376.MirrorCS", {"start": v(5.8, 6.07) * mm, "end": v(5.97, 5.74) * mm});
            skLineSegment(sketch, "E377.MirrorCS", {"start": v(6.55, -18) * mm, "end": v(6.34, -18.15) * mm});
            skLineSegment(sketch, "E378.MirrorCS", {"start": v(5.7, 6.33) * mm, "end": v(5.8, 6.07) * mm});
            skLineSegment(sketch, "E379.MirrorCS", {"start": v(0.05, -19.66) * mm, "end": v(-0.14, -19.56) * mm});
            skLineSegment(sketch, "E380.MirrorCS", {"start": v(6.71, -17.86) * mm, "end": v(6.55, -18) * mm});
            skLineSegment(sketch, "E381.MirrorCS", {"start": v(6.89, -17.68) * mm, "end": v(6.71, -17.86) * mm});
            skLineSegment(sketch, "E382.MirrorCS", {"start": v(1.98, 9.83) * mm, "end": v(2.21, 9.73) * mm});
            skLineSegment(sketch, "E383.MirrorCS", {"start": v(5.55, 6.59) * mm, "end": v(5.7, 6.33) * mm});
            skLineSegment(sketch, "E384.MirrorCS", {"start": v(-1.92, -14.78) * mm, "end": v(-1.92, -15.97) * mm});
            skLineSegment(sketch, "E385.MirrorCS", {"start": v(9.06, -13.35) * mm, "end": v(9.22, -13.07) * mm});
            skLineSegment(sketch, "E386.MirrorCS", {"start": v(9.22, -13.07) * mm, "end": v(9.39, -12.84) * mm});
            skLineSegment(sketch, "E387.MirrorCS", {"start": v(8.1, -5.45) * mm, "end": v(6.77, -5.45) * mm});
            skLineSegment(sketch, "E388.MirrorCS", {"start": v(8.1, 0) * mm, "end": v(6.77, 0) * mm});
            skLineSegment(sketch, "E389.MirrorCS", {"start": v(6.77, -5.96) * mm, "end": v(6.77, 0.83) * mm});
            skPoint(sketch, "E390.MirrorP", {"position": v(6.77, 2.07) * mm});
            skLineSegment(sketch, "E391.MirrorCS", {"start": v(-2.77, -13.1) * mm, "end": v(-2.77, -14.78) * mm});
            skLineSegment(sketch, "E392.MirrorCS", {"start": v(8.1, 0) * mm, "end": v(8.1, -5.45) * mm});
            skPoint(sketch, "E393.MirrorP", {"position": v(9.78, -10.7) * mm});
            skLineSegment(sketch, "E394.MirrorCS", {"start": v(8.7, -1.4) * mm, "end": v(8.7, -4.06) * mm});
            skLineSegment(sketch, "E395.MirrorCS", {"start": v(-1.24, -18.8) * mm, "end": v(-1.24, -16) * mm});
            skLineSegment(sketch, "E396", {"start": v(8, -0.12) * mm, "end": v(6.94, -0.12) * mm});
            skLineSegment(sketch, "E397", {"start": v(6.94, -5.26) * mm, "end": v(6.94, -0.12) * mm});
            skLineSegment(sketch, "E398", {"start": v(8, -0.12) * mm, "end": v(8, -5.26) * mm});
            skLineSegment(sketch, "E399", {"start": v(8, -5.26) * mm, "end": v(7.93, -5.26) * mm});
            skLineSegment(sketch, "E400.MirrorCS", {"start": v(-15.28, -0.12) * mm, "end": v(-14.23, -0.12) * mm});
            skLineSegment(sketch, "E401.MirrorCS", {"start": v(-14.23, -5.26) * mm, "end": v(-14.23, -0.12) * mm});
            skLineSegment(sketch, "E402.MirrorCS", {"start": v(-15.28, -0.12) * mm, "end": v(-15.28, -5.26) * mm});
            skLineSegment(sketch, "E403.MirrorCS", {"start": v(-15.28, -5.26) * mm, "end": v(-15.22, -5.26) * mm});
            skLineSegment(sketch, "E404", {"start": v(7.93, -5.26) * mm, "end": v(6.94, -5.26) * mm});
            skLineSegment(sketch, "E405.MirrorCS", {"start": v(-15.22, -5.26) * mm, "end": v(-14.23, -5.26) * mm});
            skFitSpline(sketch, "E406", {"points": [v(2.06, -10.83) * mm, v(1.95, -11.2) * mm, v(1.76, -11.47) * mm, v(1.43, -12.08) * mm, v(1.27, -12.34) * mm, v(1.08, -12.77) * mm, v(0.86, -13.23) * mm, v(0.6, -13.73) * mm, v(0.46, -14.26) * mm, v(0.26, -14.75) * mm, v(0.14, -15.2) * mm, v(0.12, -15.49) * mm, v(0.42, -15.43) * mm, v(0.93, -15.2) * mm, v(1.71, -15) * mm, v(2.83, -15) * mm, v(3.75, -15.21) * mm, v(4.5, -15.66) * mm, v(5.06, -16.32) * mm, v(5.16, -17.13) * mm, v(4.75, -17.92) * mm, v(4.2, -18.41) * mm, v(3.33, -18.8) * mm, v(2.4, -18.88) * mm, v(1.42, -18.8) * mm, v(0.68, -18.56) * mm, v(0, -18.27) * mm, v(-0.42, -18) * mm, v(-0.92, -17.96) * mm, v(-1.24, -17.97) * mm], "startDerivative": vector(-3.22, -15.07) * mm, "endDerivative": vector(-11.9, -0.4) * mm});
            skPoint(sketch, "E407.25.internal.snap0", {"position": v(-2.34, -14.78) * mm});
            skFitSpline(sketch, "E407", {"points": [v(-1.24, -17.55) * mm, v(-0.58, -17.55) * mm, v(-0.2, -17.77) * mm, v(0.5, -18.13) * mm, v(1.15, -18.39) * mm, v(1.77, -18.54) * mm, v(2.76, -18.51) * mm, v(3.36, -18.4) * mm, v(4.13, -18) * mm, v(4.57, -17.56) * mm, v(4.75, -17.2) * mm, v(4.75, -16.62) * mm, v(4.25, -16.08) * mm, v(3.61, -15.67) * mm, v(2.96, -15.42) * mm, v(2.22, -15.42) * mm, v(1.41, -15.53) * mm, v(0.84, -15.74) * mm, v(0.35, -15.92) * mm, v(0, -15.98) * mm, v(-0.35, -15.65) * mm, v(-0.76, -14.88) * mm, v(-1.14, -14.25) * mm, v(-1.46, -13.63) * mm, v(-1.9, -13.05) * mm, v(-2.34, -12.6) * mm, v(-2.86, -12.29) * mm, v(-3.44, -12.26) * mm, v(-3.65, -12.25) * mm], "startDerivative": vector(20.05, 2.02) * mm, "endDerivative": vector(-8.68, 0.97) * mm});
            skFitSpline(sketch, "E408", {"points": [v(2.06, -10.83) * mm, v(1.97, -10.83) * mm, v(1.86, -11.02) * mm, v(1.6, -11.3) * mm, v(1.4, -11.61) * mm, v(1.17, -11.94) * mm, v(0.91, -12.35) * mm, v(0.68, -12.77) * mm, v(0.44, -13.26) * mm, v(0.25, -13.82) * mm, v(0.1, -14.33) * mm, v(-0.09, -14.79) * mm, v(-0.14, -15.2) * mm, v(-0.23, -15.26) * mm, v(-0.47, -14.8) * mm, v(-0.8, -14) * mm, v(-1.15, -13.46) * mm, v(-1.39, -13.08) * mm, v(-1.69, -12.72) * mm, v(-2, -12.45) * mm, v(-2.46, -12.13) * mm, v(-2.82, -11.98) * mm, v(-3.12, -11.9) * mm, v(-3.65, -11.9) * mm], "startDerivative": vector(-4.73, 1.2) * mm, "endDerivative": vector(-11.7, -0.54) * mm});
            skEllipse(sketch, "E409", {"center": v(2.24, -16.88) * mm, "majorRadius": 1.24 * mm, "minorRadius": 1.07 * mm, "majorAxis": v(1, 0)});
            skFitSpline(sketch, "E410.MirrorCS", {"points": [v(-9.35, -10.83) * mm, v(-9.26, -10.83) * mm, v(-9.15, -11.02) * mm, v(-8.9, -11.3) * mm, v(-8.7, -11.61) * mm, v(-8.46, -11.94) * mm, v(-8.2, -12.35) * mm, v(-7.97, -12.77) * mm, v(-7.73, -13.26) * mm, v(-7.54, -13.82) * mm, v(-7.39, -14.33) * mm, v(-7.2, -14.79) * mm, v(-7.15, -15.2) * mm, v(-7.06, -15.26) * mm, v(-6.82, -14.8) * mm, v(-6.48, -14) * mm, v(-6.14, -13.46) * mm, v(-5.9, -13.08) * mm, v(-5.6, -12.72) * mm, v(-5.28, -12.45) * mm, v(-4.83, -12.13) * mm, v(-4.47, -11.98) * mm, v(-4.17, -11.9) * mm, v(-3.65, -11.9) * mm], "startDerivative": vector(4.73, 1.2) * mm, "endDerivative": vector(11.7, -0.54) * mm});
            skFitSpline(sketch, "E411.MirrorCS", {"points": [v(-9.35, -10.83) * mm, v(-9.24, -11.2) * mm, v(-9.05, -11.47) * mm, v(-8.72, -12.08) * mm, v(-8.57, -12.34) * mm, v(-8.37, -12.77) * mm, v(-8.15, -13.23) * mm, v(-7.88, -13.73) * mm, v(-7.75, -14.26) * mm, v(-7.55, -14.75) * mm, v(-7.43, -15.2) * mm, v(-7.4, -15.49) * mm, v(-7.7, -15.43) * mm, v(-8.22, -15.2) * mm, v(-9, -15) * mm, v(-10.12, -15) * mm, v(-11.04, -15.21) * mm, v(-11.78, -15.66) * mm, v(-12.35, -16.32) * mm, v(-12.45, -17.13) * mm, v(-12.04, -17.92) * mm, v(-11.5, -18.41) * mm, v(-10.62, -18.8) * mm, v(-9.7, -18.88) * mm, v(-8.72, -18.8) * mm, v(-7.97, -18.56) * mm, v(-7.3, -18.27) * mm, v(-6.87, -18) * mm, v(-6.37, -17.96) * mm, v(-6.05, -17.97) * mm], "startDerivative": vector(3.22, -15.07) * mm, "endDerivative": vector(11.9, -0.4) * mm});
            skFitSpline(sketch, "E412.MirrorCS", {"points": [v(-6.05, -17.55) * mm, v(-6.71, -17.55) * mm, v(-7.1, -17.77) * mm, v(-7.79, -18.13) * mm, v(-8.44, -18.39) * mm, v(-9.06, -18.54) * mm, v(-10.05, -18.51) * mm, v(-10.66, -18.4) * mm, v(-11.42, -18) * mm, v(-11.86, -17.56) * mm, v(-12.04, -17.2) * mm, v(-12.04, -16.62) * mm, v(-11.55, -16.08) * mm, v(-10.9, -15.67) * mm, v(-10.25, -15.42) * mm, v(-9.5, -15.42) * mm, v(-8.7, -15.53) * mm, v(-8.13, -15.74) * mm, v(-7.64, -15.92) * mm, v(-7.3, -15.98) * mm, v(-6.94, -15.65) * mm, v(-6.53, -14.88) * mm, v(-6.15, -14.25) * mm, v(-5.83, -13.63) * mm, v(-5.39, -13.05) * mm, v(-4.95, -12.6) * mm, v(-4.43, -12.29) * mm, v(-3.85, -12.26) * mm, v(-3.65, -12.25) * mm], "startDerivative": vector(-20.05, 2.02) * mm, "endDerivative": vector(8.68, 0.97) * mm});
            skEllipse(sketch, "E413.MirrorC", {"center": v(-9.53, -16.88) * mm, "majorRadius": 1.24 * mm, "minorRadius": 1.07 * mm, "majorAxis": v(-1, 0)});
            skSolve(sketch);
        }
        {
            var Q0;
            Q0=qCreatedBy(makeId("Front.planeOp"),FACE);
            var sketch = newSketch(context, id + "F1", { "sketchPlane" : qUnion([Q0])});
            skFitSpline(sketch, "E414", {"points": [v(-13.37, -3.82) * mm, v(-13.22, -4.24) * mm, v(-13, -4.71) * mm, v(-12.62, -5.23) * mm, v(-12.22, -5.53) * mm, v(-11.85, -5.77) * mm, v(-11.27, -5.82) * mm, v(-10.75, -5.78) * mm, v(-10.31, -5.59) * mm, v(-9.9, -5.34) * mm, v(-9.31, -4.94) * mm, v(-8.76, -4.52) * mm, v(-8.29, -4.14) * mm, v(-7.54, -3.42) * mm, v(-6.76, -2.66) * mm, v(-5.84, -1.87) * mm, v(-5.04, -1.12) * mm, v(-4.36, -0.77) * mm, v(-4.22, -0.66) * mm, v(-4.44, -0.55) * mm, v(-5.36, -0.98) * mm, v(-6.56, -2.11) * mm, v(-8.28, -3.59) * mm, v(-9.63, -4.62) * mm, v(-10.38, -5.05) * mm, v(-10.9, -5.15) * mm, v(-11.48, -5.16) * mm, v(-11.88, -5.1) * mm, v(-12.26, -4.82) * mm, v(-12.7, -4.37) * mm, v(-13.02, -3.89) * mm, v(-13.37, -3.82) * mm]});
            skFitSpline(sketch, "E415", {"points": [v(-12.63, -0.05) * mm, v(-12.86, -0.55) * mm, v(-12.8, -1.32) * mm, v(-12.63, -2.05) * mm, v(-12.36, -2.56) * mm, v(-12, -3.13) * mm, v(-11.66, -3.42) * mm, v(-11.2, -3.47) * mm, v(-10.62, -3.42) * mm, v(-10.14, -3.26) * mm, v(-9.7, -3.07) * mm, v(-9.22, -2.83) * mm, v(-8.76, -2.55) * mm, v(-8.32, -2.3) * mm, v(-7.8, -1.92) * mm, v(-7.35, -1.64) * mm, v(-6.91, -1.32) * mm, v(-6.48, -0.95) * mm, v(-5.93, -0.57) * mm, v(-5.85, -0.28) * mm, v(-6.03, 0) * mm, v(-6.47, 0) * mm, v(-12.55, 0) * mm, v(-12.63, -0.05) * mm]});
            skFitSpline(sketch, "E416", {"points": [v(-16.06, -8.18) * mm, v(-16.1, -8.46) * mm, v(-16.05, -8.95) * mm, v(-16.01, -9.37) * mm, v(-15.9, -9.9) * mm, v(-15.75, -10.31) * mm, v(-15.36, -11.02) * mm, v(-14.78, -11.66) * mm, v(-14.6, -11.72) * mm, v(-14.4, -11.4) * mm, v(-13.9, -10.88) * mm, v(-13.32, -10.49) * mm, v(-12.97, -10.47) * mm, v(-12.95, -10.32) * mm, v(-13.25, -10.02) * mm, v(-13.78, -9.54) * mm, v(-14.13, -8.98) * mm, v(-14.42, -8.5) * mm, v(-14.5, -7.78) * mm, v(-14.62, -7.5) * mm, v(-14.66, -7.16) * mm, v(-14.9, -7.2) * mm, v(-16.06, -8.18) * mm]});
            skFitSpline(sketch, "E417", {"points": [v(-15.36, -14.22) * mm, v(-15.25, -13.78) * mm, v(-15.08, -13.48) * mm, v(-14.87, -13.16) * mm, v(-14.53, -12.8) * mm, v(-14.23, -12.48) * mm, v(-13.86, -12.17) * mm, v(-13.47, -11.87) * mm, v(-12.98, -11.62) * mm, v(-12.45, -11.34) * mm, v(-11.95, -11.1) * mm, v(-11.13, -10.82) * mm, v(-10.51, -10.65) * mm, v(-10.22, -10.58) * mm, v(-10.44, -10.47) * mm, v(-10.85, -10.24) * mm, v(-11.27, -10.04) * mm, v(-11.72, -9.79) * mm, v(-12.1, -9.58) * mm, v(-12.4, -9.35) * mm, v(-12.71, -9.1) * mm, v(-12.95, -8.83) * mm, v(-13.19, -8.64) * mm, v(-13.38, -8.34) * mm, v(-13.56, -8.07) * mm, v(-13.8, -7.58) * mm, v(-13.95, -7.1) * mm, v(-14, -6.57) * mm, v(-14.04, -6.12) * mm], "startDerivative": vector(2.36, 12.9) * mm, "endDerivative": vector(-1.23, 12.29) * mm});
            skFitSpline(sketch, "E418", {"points": [v(-13.8, 0.84) * mm, v(-13.8, -6.1) * mm], "startDerivative": vector(0, -6.93) * mm, "endDerivative": vector(0, -6.93) * mm});
            skFitSpline(sketch, "E419", {"points": [v(-14.06, 0.84) * mm, v(-14.04, -5.91) * mm], "startDerivative": vector(0.02, -6.76) * mm, "endDerivative": vector(0.02, -6.76) * mm});
            skFitSpline(sketch, "E420", {"points": [v(-13.8, -6.1) * mm, v(-13.73, -6.5) * mm, v(-13.66, -7.04) * mm, v(-13.5, -7.5) * mm, v(-13.28, -7.91) * mm, v(-13.02, -8.24) * mm, v(-12.68, -8.57) * mm, v(-12.3, -8.83) * mm, v(-11.92, -9.09) * mm, v(-11.48, -9.4) * mm, v(-10.93, -9.7) * mm, v(-10.6, -9.9) * mm, v(-10.2, -10.13) * mm, v(-9.88, -10.37) * mm, v(-9.74, -10.51) * mm, v(-8.96, -9.9) * mm, v(-8.3, -9.2) * mm, v(-7.6, -8.47) * mm, v(-7.18, -8.08) * mm, v(-6.67, -7.6) * mm, v(-6.02, -7.1) * mm, v(-5.3, -6.62) * mm, v(-4.73, -6.22) * mm, v(-4.23, -6.1) * mm, v(-3.67, -6.1) * mm], "startDerivative": vector(2.3, -10.83) * mm, "endDerivative": vector(13.65, -0.46) * mm});
            skFitSpline(sketch, "E421", {"points": [v(-15.04, -14.45) * mm, v(-14.93, -14.06) * mm, v(-14.8, -13.81) * mm, v(-14.6, -13.51) * mm, v(-14.4, -13.26) * mm, v(-14.15, -13) * mm, v(-13.9, -12.75) * mm, v(-13.6, -12.5) * mm, v(-13.27, -12.22) * mm, v(-12.84, -11.94) * mm, v(-12.35, -11.69) * mm, v(-11.95, -11.49) * mm, v(-11.53, -11.32) * mm, v(-11.06, -11.16) * mm, v(-10.6, -11.05) * mm, v(-10.23, -10.96) * mm, v(-9.83, -10.86) * mm, v(-9.4, -10.72) * mm, v(-8.8, -10.37) * mm, v(-8.17, -9.89) * mm, v(-7.53, -9.47) * mm, v(-6.83, -9.07) * mm, v(-6.18, -8.75) * mm, v(-5.5, -8.5) * mm, v(-4.99, -8.44) * mm, v(-4.39, -8.44) * mm, v(-3.94, -8.44) * mm, v(-3.64, -8.44) * mm], "startDerivative": vector(2.94, 12.22) * mm, "endDerivative": vector(10, -0.02) * mm});
            skLineSegment(sketch, "E422", {"start": v(-8.95, -10.2) * mm, "end": v(-8.3, -9.79) * mm});
            skLineSegment(sketch, "E423", {"start": v(-8.3, -9.79) * mm, "end": v(-8.3, -9.53) * mm});
            skLineSegment(sketch, "E424", {"start": v(-8.3, -9.53) * mm, "end": v(-8.95, -10.2) * mm});
            skLineSegment(sketch, "E425", {"start": v(-7.34, -8.5) * mm, "end": v(-7.34, -9.12) * mm});
            skLineSegment(sketch, "E426", {"start": v(-7.34, -9.12) * mm, "end": v(-6.55, -8.7) * mm});
            skLineSegment(sketch, "E427", {"start": v(-6.55, -8.7) * mm, "end": v(-6.55, -7.98) * mm});
            skLineSegment(sketch, "E428", {"start": v(-6.55, -7.98) * mm, "end": v(-7.34, -8.5) * mm});
            skLineSegment(sketch, "E429", {"start": v(-5.76, -7.24) * mm, "end": v(-5.76, -8.1) * mm});
            skLineSegment(sketch, "E430", {"start": v(-5.76, -8.1) * mm, "end": v(-5.04, -8.1) * mm});
            skLineSegment(sketch, "E431", {"start": v(-5.04, -8.1) * mm, "end": v(-5.04, -6.89) * mm});
            skLineSegment(sketch, "E432", {"start": v(-5.04, -6.89) * mm, "end": v(-5.76, -7.24) * mm});
            skLineSegment(sketch, "E433", {"start": v(-4.1, -6.42) * mm, "end": v(-4.1, -7.95) * mm});
            skLineSegment(sketch, "E434", {"start": v(-4.1, -7.95) * mm, "end": v(-3.67, -7.95) * mm});
            skLineSegment(sketch, "E435", {"start": v(-4.1, -6.42) * mm, "end": v(-3.65, -6.42) * mm});
            skLineSegment(sketch, "E436", {"start": v(-13.8, 0.84) * mm, "end": v(-3.64, 0.84) * mm});
            skLineSegment(sketch, "E437", {"start": v(-15.36, -14.22) * mm, "end": v(-15.04, -14.45) * mm});
            skLineSegment(sketch, "E438", {"start": v(-3.64, 0.84) * mm, "end": v(-3.64, -15.75) * mm});
            skLineSegment(sketch, "E439.MirrorCS", {"start": v(-0.72, -8.7) * mm, "end": v(-0.72, -7.98) * mm});
            skLineSegment(sketch, "E440.MirrorCS", {"start": v(-0.72, -7.98) * mm, "end": v(0.07, -8.5) * mm});
            skLineSegment(sketch, "E441.MirrorCS", {"start": v(8.08, -14.22) * mm, "end": v(7.77, -14.45) * mm});
            skLineSegment(sketch, "E442.MirrorCS", {"start": v(-3.18, -7.95) * mm, "end": v(-3.6, -7.95) * mm});
            skLineSegment(sketch, "E443.MirrorCS", {"start": v(0.07, -8.5) * mm, "end": v(0.07, -9.12) * mm});
            skLineSegment(sketch, "E444.MirrorCS", {"start": v(-3.18, -6.42) * mm, "end": v(-3.62, -6.42) * mm});
            skLineSegment(sketch, "E445.MirrorCS", {"start": v(1.03, -9.79) * mm, "end": v(1.03, -9.53) * mm});
            skLineSegment(sketch, "E446.MirrorCS", {"start": v(1.68, -10.2) * mm, "end": v(1.03, -9.79) * mm});
            skLineSegment(sketch, "E447.MirrorCS", {"start": v(1.03, -9.53) * mm, "end": v(1.68, -10.2) * mm});
            skLineSegment(sketch, "E448.MirrorCS", {"start": v(-2.23, -8.1) * mm, "end": v(-2.23, -6.89) * mm});
            skLineSegment(sketch, "E449.MirrorCS", {"start": v(-1.51, -7.24) * mm, "end": v(-1.51, -8.1) * mm});
            skLineSegment(sketch, "E450.MirrorCS", {"start": v(-2.23, -6.89) * mm, "end": v(-1.51, -7.24) * mm});
            skLineSegment(sketch, "E451.MirrorCS", {"start": v(0.07, -9.12) * mm, "end": v(-0.72, -8.7) * mm});
            skLineSegment(sketch, "E452.MirrorCS", {"start": v(-1.51, -8.1) * mm, "end": v(-2.23, -8.1) * mm});
            skFitSpline(sketch, "E453.MirrorCS", {"points": [v(8.08, -14.22) * mm, v(7.98, -13.78) * mm, v(7.81, -13.48) * mm, v(7.6, -13.16) * mm, v(7.25, -12.8) * mm, v(6.96, -12.48) * mm, v(6.6, -12.17) * mm, v(6.2, -11.87) * mm, v(5.7, -11.62) * mm, v(5.18, -11.34) * mm, v(4.68, -11.1) * mm, v(3.85, -10.82) * mm, v(3.24, -10.65) * mm, v(2.95, -10.58) * mm, v(3.17, -10.47) * mm, v(3.58, -10.24) * mm, v(4, -10.04) * mm, v(4.45, -9.79) * mm, v(4.82, -9.58) * mm, v(5.14, -9.35) * mm, v(5.44, -9.1) * mm, v(5.68, -8.83) * mm, v(5.92, -8.64) * mm, v(6.1, -8.34) * mm, v(6.3, -8.07) * mm, v(6.53, -7.58) * mm, v(6.68, -7.1) * mm, v(6.73, -6.57) * mm, v(6.77, -6.12) * mm], "startDerivative": vector(-2.36, 12.9) * mm, "endDerivative": vector(1.23, 12.29) * mm});
            skFitSpline(sketch, "E454.MirrorCS", {"points": [v(6.53, -6.1) * mm, v(6.46, -6.5) * mm, v(6.38, -7.04) * mm, v(6.22, -7.5) * mm, v(6, -7.91) * mm, v(5.75, -8.24) * mm, v(5.41, -8.57) * mm, v(5.03, -8.83) * mm, v(4.65, -9.09) * mm, v(4.2, -9.4) * mm, v(3.65, -9.7) * mm, v(3.32, -9.9) * mm, v(2.92, -10.13) * mm, v(2.6, -10.37) * mm, v(2.47, -10.51) * mm, v(1.69, -9.9) * mm, v(1.02, -9.2) * mm, v(0.34, -8.47) * mm, v(-0.09, -8.08) * mm, v(-0.6, -7.6) * mm, v(-1.25, -7.1) * mm, v(-1.98, -6.62) * mm, v(-2.54, -6.22) * mm, v(-3.04, -6.1) * mm, v(-3.6, -6.1) * mm], "startDerivative": vector(-2.3, -10.83) * mm, "endDerivative": vector(-13.65, -0.46) * mm});
            skFitSpline(sketch, "E455.MirrorCS", {"points": [v(7.77, -14.45) * mm, v(7.66, -14.06) * mm, v(7.52, -13.81) * mm, v(7.32, -13.51) * mm, v(7.13, -13.26) * mm, v(6.88, -13) * mm, v(6.62, -12.75) * mm, v(6.33, -12.5) * mm, v(6, -12.22) * mm, v(5.57, -11.94) * mm, v(5.07, -11.69) * mm, v(4.68, -11.49) * mm, v(4.26, -11.32) * mm, v(3.8, -11.16) * mm, v(3.33, -11.05) * mm, v(2.96, -10.96) * mm, v(2.56, -10.86) * mm, v(2.14, -10.72) * mm, v(1.53, -10.37) * mm, v(0.9, -9.89) * mm, v(0.25, -9.47) * mm, v(-0.44, -9.07) * mm, v(-1.1, -8.75) * mm, v(-1.76, -8.5) * mm, v(-2.29, -8.44) * mm, v(-2.89, -8.44) * mm, v(-3.33, -8.44) * mm, v(-3.63, -8.44) * mm], "startDerivative": vector(-2.94, 12.22) * mm, "endDerivative": vector(-10, -0.02) * mm});
            skFitSpline(sketch, "E456.MirrorC", {"points": [v(6.1, -3.82) * mm, v(5.95, -4.24) * mm, v(5.72, -4.71) * mm, v(5.35, -5.23) * mm, v(4.95, -5.53) * mm, v(4.58, -5.77) * mm, v(4, -5.82) * mm, v(3.48, -5.78) * mm, v(3.04, -5.59) * mm, v(2.62, -5.34) * mm, v(2.04, -4.94) * mm, v(1.49, -4.52) * mm, v(1.01, -4.14) * mm, v(0.27, -3.42) * mm, v(-0.52, -2.66) * mm, v(-1.43, -1.87) * mm, v(-2.24, -1.12) * mm, v(-2.92, -0.77) * mm, v(-3.05, -0.66) * mm, v(-2.83, -0.55) * mm, v(-1.9, -0.98) * mm, v(-0.71, -2.11) * mm, v(1, -3.59) * mm, v(2.36, -4.62) * mm, v(3.1, -5.05) * mm, v(3.63, -5.15) * mm, v(4.21, -5.16) * mm, v(4.6, -5.1) * mm, v(4.99, -4.82) * mm, v(5.43, -4.37) * mm, v(5.75, -3.89) * mm, v(6.1, -3.82) * mm]});
            skFitSpline(sketch, "E457.MirrorC", {"points": [v(5.36, -0.05) * mm, v(5.58, -0.55) * mm, v(5.54, -1.32) * mm, v(5.36, -2.05) * mm, v(5.1, -2.56) * mm, v(4.73, -3.13) * mm, v(4.4, -3.42) * mm, v(3.92, -3.47) * mm, v(3.35, -3.42) * mm, v(2.87, -3.26) * mm, v(2.44, -3.07) * mm, v(1.95, -2.83) * mm, v(1.5, -2.55) * mm, v(1.05, -2.3) * mm, v(0.53, -1.92) * mm, v(0.08, -1.64) * mm, v(-0.36, -1.32) * mm, v(-0.8, -0.95) * mm, v(-1.35, -0.57) * mm, v(-1.42, -0.28) * mm, v(-1.24, 0) * mm, v(-0.8, 0) * mm, v(5.28, 0) * mm, v(5.36, -0.05) * mm]});
            skFitSpline(sketch, "E458.MirrorC", {"points": [v(8.79, -8.18) * mm, v(8.82, -8.46) * mm, v(8.78, -8.95) * mm, v(8.74, -9.37) * mm, v(8.64, -9.9) * mm, v(8.48, -10.31) * mm, v(8.08, -11.02) * mm, v(7.5, -11.66) * mm, v(7.32, -11.72) * mm, v(7.13, -11.4) * mm, v(6.62, -10.88) * mm, v(6.05, -10.49) * mm, v(5.7, -10.47) * mm, v(5.68, -10.32) * mm, v(5.98, -10.02) * mm, v(6.51, -9.54) * mm, v(6.86, -8.98) * mm, v(7.15, -8.5) * mm, v(7.24, -7.78) * mm, v(7.35, -7.5) * mm, v(7.38, -7.16) * mm, v(7.63, -7.2) * mm, v(8.79, -8.18) * mm]});
            skLineSegment(sketch, "E459.MirrorCS", {"start": v(6.53, 0.84) * mm, "end": v(-3.64, 0.84) * mm});
            skFitSpline(sketch, "E460.MirrorCS", {"points": [v(6.8, 0.84) * mm, v(6.77, -5.91) * mm], "startDerivative": vector(-0.02, -6.76) * mm, "endDerivative": vector(-0.02, -6.76) * mm});
            skLineSegment(sketch, "E461.MirrorCS", {"start": v(-3.18, -6.42) * mm, "end": v(-3.18, -7.95) * mm});
            skFitSpline(sketch, "E462.MirrorCS", {"points": [v(6.53, 0.84) * mm, v(6.53, -6.1) * mm], "startDerivative": vector(0, -6.93) * mm, "endDerivative": vector(0, -6.93) * mm});
            skLineSegment(sketch, "E463", {"start": v(6.77, -6.12) * mm, "end": v(6.53, -6.1) * mm});
            skLineSegment(sketch, "E464", {"start": v(-13.8, -6.1) * mm, "end": v(-14.04, -6.12) * mm});
            skLineSegment(sketch, "E465", {"start": v(-3.63, -8.44) * mm, "end": v(-3.64, -8.44) * mm});
            skLineSegment(sketch, "E466", {"start": v(-3.6, -6.1) * mm, "end": v(-3.67, -6.1) * mm});
            skLineSegment(sketch, "E467", {"start": v(-3.65, -6.42) * mm, "end": v(-3.62, -6.42) * mm});
            skLineSegment(sketch, "E468", {"start": v(-3.6, -7.95) * mm, "end": v(-3.67, -7.95) * mm});
            skLineSegment(sketch, "E469", {"start": v(-3.64, 2.09) * mm, "end": v(-3.64, 11.48) * mm});
            skLineSegment(sketch, "E470", {"start": v(6.52, 2.09) * mm, "end": v(-3.64, 2.09) * mm});
            skLineSegment(sketch, "E471", {"start": v(6.79, 2.09) * mm, "end": v(7.13, 2.09) * mm});
            skLineSegment(sketch, "E472", {"start": v(7.13, 0.84) * mm, "end": v(6.8, 0.84) * mm});
            skLineSegment(sketch, "E473", {"start": v(7.2, 0.95) * mm, "end": v(7.2, 2) * mm});
            skFitSpline(sketch, "E474", {"points": [v(7.2, 1.92) * mm, v(7.2, 2) * mm, v(7.13, 2.09) * mm, v(7.04, 2.09) * mm], "startDerivative": vector(0.04, 0.25) * mm, "endDerivative": vector(-0.27, -0.06) * mm});
            skFitSpline(sketch, "E475", {"points": [v(7.04, 0.84) * mm, v(7.13, 0.84) * mm, v(7.2, 0.95) * mm, v(7.2, 1.07) * mm], "startDerivative": vector(0.9, 0.06) * mm, "endDerivative": vector(-0.04, 0.34) * mm});
            skFitSpline(sketch, "E476", {"points": [v(6.52, 2.09) * mm, v(6.52, 2.46) * mm, v(6.45, 2.98) * mm, v(6.36, 3.6) * mm, v(6.14, 4.28) * mm, v(5.85, 5) * mm, v(5.67, 5.55) * mm, v(5.37, 6.14) * mm, v(5.03, 6.76) * mm, v(4.61, 7.36) * mm, v(4.2, 7.84) * mm, v(3.75, 8.29) * mm, v(3.21, 8.76) * mm, v(2.78, 9.1) * mm, v(2.24, 9.43) * mm, v(1.66, 9.69) * mm, v(1.12, 9.9) * mm, v(0.65, 10.08) * mm, v(0, 10.28) * mm, v(-0.73, 10.5) * mm, v(-1.5, 10.55) * mm, v(-2.25, 10.67) * mm, v(-3.14, 10.72) * mm, v(-3.64, 10.75) * mm], "startDerivative": vector(0.46, 10.68) * mm, "endDerivative": vector(-11.79, 0.9) * mm});
            skFitSpline(sketch, "E477", {"points": [v(-3.64, 11.26) * mm, v(-2.76, 11.27) * mm, v(-1.88, 11.2) * mm, v(-0.74, 10.95) * mm, v(0.33, 10.72) * mm, v(1.45, 10.35) * mm, v(2.57, 9.83) * mm, v(3.17, 9.4) * mm, v(3.63, 9.04) * mm, v(4.14, 8.44) * mm], "startDerivative": vector(8.22, 0.23) * mm, "endDerivative": vector(5.05, -6.42) * mm});
            skFitSpline(sketch, "E478", {"points": [v(4.14, 8.44) * mm, v(4.48, 8.14) * mm, v(4.97, 7.6) * mm, v(5.57, 6.69) * mm, v(5.94, 5.94) * mm, v(6.28, 4.96) * mm, v(6.52, 4.28) * mm, v(6.62, 3.74) * mm, v(6.75, 3.09) * mm, v(6.8, 2.65) * mm, v(6.79, 2.09) * mm], "startDerivative": vector(4.13, -3.43) * mm, "endDerivative": vector(-0.38, -6.57) * mm});
            skLineSegment(sketch, "E479.MirrorCS", {"start": v(-13.8, 2.09) * mm, "end": v(-3.64, 2.09) * mm});
            skLineSegment(sketch, "E480.MirrorCS", {"start": v(-14.4, 0.84) * mm, "end": v(-14.06, 0.84) * mm});
            skFitSpline(sketch, "E481.MirrorCS", {"points": [v(-14.31, 0.84) * mm, v(-14.4, 0.84) * mm, v(-14.46, 0.95) * mm, v(-14.46, 1.07) * mm], "startDerivative": vector(-0.9, 0.06) * mm, "endDerivative": vector(0.04, 0.34) * mm});
            skLineSegment(sketch, "E482.MirrorCS", {"start": v(-14.46, 0.95) * mm, "end": v(-14.46, 2) * mm});
            skFitSpline(sketch, "E483.MirrorCS", {"points": [v(-14.46, 1.92) * mm, v(-14.46, 2) * mm, v(-14.4, 2.09) * mm, v(-14.31, 2.09) * mm], "startDerivative": vector(-0.04, 0.25) * mm, "endDerivative": vector(0.27, -0.06) * mm});
            skLineSegment(sketch, "E484.MirrorCS", {"start": v(-14.06, 2.09) * mm, "end": v(-14.4, 2.09) * mm});
            skFitSpline(sketch, "E485.MirrorCS", {"points": [v(-13.8, 2.09) * mm, v(-13.8, 2.46) * mm, v(-13.72, 2.98) * mm, v(-13.63, 3.6) * mm, v(-13.4, 4.28) * mm, v(-13.12, 5) * mm, v(-12.94, 5.55) * mm, v(-12.64, 6.14) * mm, v(-12.3, 6.76) * mm, v(-11.88, 7.36) * mm, v(-11.48, 7.84) * mm, v(-11.02, 8.29) * mm, v(-10.48, 8.76) * mm, v(-10.06, 9.1) * mm, v(-9.52, 9.43) * mm, v(-8.93, 9.69) * mm, v(-8.4, 9.9) * mm, v(-7.92, 10.08) * mm, v(-7.27, 10.28) * mm, v(-6.54, 10.5) * mm, v(-5.77, 10.55) * mm, v(-5.02, 10.67) * mm, v(-4.13, 10.72) * mm, v(-3.64, 10.75) * mm], "startDerivative": vector(-0.46, 10.68) * mm, "endDerivative": vector(11.79, 0.9) * mm});
            skFitSpline(sketch, "E486.MirrorCS", {"points": [v(-11.41, 8.44) * mm, v(-11.76, 8.14) * mm, v(-12.24, 7.6) * mm, v(-12.85, 6.69) * mm, v(-13.2, 5.94) * mm, v(-13.55, 4.96) * mm, v(-13.8, 4.28) * mm, v(-13.9, 3.74) * mm, v(-14.02, 3.09) * mm, v(-14.08, 2.65) * mm, v(-14.06, 2.09) * mm], "startDerivative": vector(-4.13, -3.43) * mm, "endDerivative": vector(0.38, -6.57) * mm});
            skFitSpline(sketch, "E487.MirrorCS", {"points": [v(-3.64, 11.26) * mm, v(-4.5, 11.27) * mm, v(-5.4, 11.2) * mm, v(-6.54, 10.95) * mm, v(-7.6, 10.72) * mm, v(-8.73, 10.35) * mm, v(-9.84, 9.83) * mm, v(-10.45, 9.4) * mm, v(-10.9, 9.04) * mm, v(-11.41, 8.44) * mm], "startDerivative": vector(-8.22, 0.23) * mm, "endDerivative": vector(-5.05, -6.42) * mm});
            skLineSegment(sketch, "E488", {"start": v(6.77, -5.91) * mm, "end": v(6.77, -6.12) * mm});
            skLineSegment(sketch, "E489", {"start": v(-14.04, -5.91) * mm, "end": v(-14.04, -6.12) * mm});
            skSolve(sketch);
        }
        {
            var Q0;
            Q0 = qSketchRegion(id + "F0", true);
            var Q1;
            Q1=makeQuery(id+"F0.imprint","IMPRINT",FACE,{"disambiguationData":[TD([[makeQuery(id+"F0.imprint","IMPRINT",EDGE,{"derivedFrom":sQuery(id+"F0.wireOp",EDGE,"E396")}),1.0]])]});
            var Q2;
            Q2=makeQuery(id+"F0.imprint","IMPRINT",FACE,{"disambiguationData":[TD([[makeQuery(id+"F0.imprint","IMPRINT",EDGE,{"derivedFrom":sQuery(id+"F0.wireOp",EDGE,"E400.MirrorCS")}),-1.0]])]});
            var Q3;
            {var subQ3=sQuery(id+"F0.wireOp",EDGE,"E190");Q3=makeQuery(id+"F0.imprint","IMPRINT",FACE,{"disambiguationData":[TD([[makeQuery(id+"F0.imprint","IMPRINT",EDGE,{"derivedFrom":subQ3}),-1.0]])]});}
            var Q4;
            Q4=makeQuery(id+"F0.imprint","IMPRINT",FACE,{"disambiguationData":[TD([[makeQuery(id+"F0.imprint","IMPRINT",EDGE,{"derivedFrom":sQuery(id+"F0.wireOp",EDGE,"E334.MirrorCS")}),1.0]])]});
            var Q5;
            {var subQ1=sQuery(id+"F0.wireOp",EDGE,"E410.MirrorCS");Q5=makeQuery(id+"F0.imprint","IMPRINT",FACE,{"disambiguationData":[TD([[makeQuery(id+"F0.imprint","IMPRINT",EDGE,{"derivedFrom":subQ1}),-1.0]])]});}
            var Q6;
            {var subQ1=sQuery(id+"F0.wireOp",EDGE,"E406");Q6=makeQuery(id+"F0.imprint","IMPRINT",FACE,{"disambiguationData":[TD([[makeQuery(id+"F0.imprint","IMPRINT",EDGE,{"derivedFrom":subQ1}),-1.0]])]});}
            var Q7;
            Q7=makeQuery(id+"F0.imprint","IMPRINT",FACE,{"disambiguationData":[TD([[makeQuery(id+"F0.imprint","IMPRINT",EDGE,{"derivedFrom":sQuery(id+"F0.wireOp",EDGE,"E409")}),1.0]])]});
            var Q8;
            Q8=makeQuery(id+"F0.imprint","IMPRINT",FACE,{"disambiguationData":[TD([[makeQuery(id+"F0.imprint","IMPRINT",EDGE,{"derivedFrom":sQuery(id+"F0.wireOp",EDGE,"E413.MirrorC")}),1.0]])]});
            extrude(context, id + "F2", {"entities" : qUnion([Q0, Q1, Q2, Q3, Q4, Q5, Q6, Q7, Q8]), "depth" : 3 * mm});
        }
        {
            var Q0;
            Q0=makeQuery(id+"F1.imprint","IMPRINT",FACE,{"disambiguationData":[TD([[makeQuery(id+"F1.imprint","IMPRINT",EDGE,{"derivedFrom":sQuery(id+"F1.wireOp",EDGE,"E457.MirrorC")}),-1.0]])]});
            var Q1;
            Q1=makeQuery(id+"F1.imprint","IMPRINT",FACE,{"disambiguationData":[TD([[makeQuery(id+"F1.imprint","IMPRINT",EDGE,{"derivedFrom":sQuery(id+"F1.wireOp",EDGE,"E415")}),1.0]])]});
            var Q2;
            Q2=makeQuery(id+"F1.imprint","IMPRINT",FACE,{"disambiguationData":[TD([[makeQuery(id+"F1.imprint","IMPRINT",EDGE,{"derivedFrom":sQuery(id+"F1.wireOp",EDGE,"E414")}),1.0]])]});
            var Q3;
            Q3=makeQuery(id+"F1.imprint","IMPRINT",FACE,{"disambiguationData":[TD([[makeQuery(id+"F1.imprint","IMPRINT",EDGE,{"derivedFrom":sQuery(id+"F1.wireOp",EDGE,"E456.MirrorC")}),-1.0]])]});
            var Q4;
            Q4=makeQuery(id+"F1.imprint","IMPRINT",FACE,{"disambiguationData":[TD([[makeQuery(id+"F1.imprint","IMPRINT",EDGE,{"derivedFrom":sQuery(id+"F1.wireOp",EDGE,"E458.MirrorC")}),-1.0]])]});
            var Q5;
            Q5=makeQuery(id+"F1.imprint","IMPRINT",FACE,{"disambiguationData":[TD([[makeQuery(id+"F1.imprint","IMPRINT",EDGE,{"derivedFrom":sQuery(id+"F1.wireOp",EDGE,"E416")}),1.0]])]});
            var Q6;
            Q6=makeQuery(id+"F0.imprint","IMPRINT",FACE,{"disambiguationData":[TD([[makeQuery(id+"F0.imprint","IMPRINT",EDGE,{"derivedFrom":sQuery(id+"F0.wireOp",EDGE,"E396")}),1.0]])]});
            var Q7;
            Q7=makeQuery(id+"F0.imprint","IMPRINT",FACE,{"disambiguationData":[TD([[makeQuery(id+"F0.imprint","IMPRINT",EDGE,{"derivedFrom":sQuery(id+"F0.wireOp",EDGE,"E400.MirrorCS")}),-1.0]])]});
            extrude(context, id + "F3", {"entities" : qUnion([Q0, Q1, Q2, Q3, Q4, Q5, Q6, Q7]), "operationType" : NewBodyOperationType.REMOVE, "depth" : 1 * mm});
        }
        {
            var Q0;
            Q0=makeQuery(id+"F3.boolean.opBoolean","COPY",FACE,{"derivedFrom":makeQuery(id+"F3.opExtrude","CAP_FACE",FACE,{"disambiguationData":[OSD([sQuery(id+"F0.wireOp",EDGE,"E90"),sQuery(id+"F0.wireOp",EDGE,"E91"),sQuery(id+"F0.wireOp",EDGE,"E92"),sQuery(id+"F0.wireOp",EDGE,"E93"),sQuery(id+"F0.wireOp",EDGE,"E94"),sQuery(id+"F0.wireOp",EDGE,"E190"),sQuery(id+"F0.wireOp",EDGE,"E191"),sQuery(id+"F0.wireOp",EDGE,"E192"),sQuery(id+"F0.wireOp",EDGE,"E193"),sQuery(id+"F0.wireOp",EDGE,"E194"),sQuery(id+"F0.wireOp",EDGE,"E195"),sQuery(id+"F0.wireOp",EDGE,"E196"),sQuery(id+"F0.wireOp",EDGE,"E197"),sQuery(id+"F0.wireOp",EDGE,"E285.MirrorCS"),sQuery(id+"F0.wireOp",EDGE,"E287.MirrorCS"),sQuery(id+"F0.wireOp",EDGE,"E334.MirrorCS"),sQuery(id+"F0.wireOp",EDGE,"E340.MirrorCS"),sQuery(id+"F0.wireOp",EDGE,"E341.MirrorCS"),sQuery(id+"F0.wireOp",EDGE,"E345.MirrorCS"),sQuery(id+"F0.wireOp",EDGE,"E348.MirrorCS"),sQuery(id+"F0.wireOp",EDGE,"E352.MirrorCS"),sQuery(id+"F0.wireOp",EDGE,"E362.MirrorCS"),sQuery(id+"F0.wireOp",EDGE,"E371.MirrorCS"),sQuery(id+"F0.wireOp",EDGE,"E384.MirrorCS"),sQuery(id+"F0.wireOp",EDGE,"E391.MirrorCS"),sQuery(id+"F0.wireOp",EDGE,"E395.MirrorCS")])],"isStart":false})});
            var Q1;
            Q1=makeQuery(id+"F1.imprint","IMPRINT",FACE,{"disambiguationData":[TD([[makeQuery(id+"F1.imprint","IMPRINT",EDGE,{"derivedFrom":sQuery(id+"F1.wireOp",EDGE,"E418")}),-1.0]])]});
            var Q2;
            Q2=makeQuery(id+"F1.imprint","IMPRINT",FACE,{"disambiguationData":[TD([[makeQuery(id+"F1.imprint","IMPRINT",EDGE,{"derivedFrom":sQuery(id+"F1.wireOp",EDGE,"E439.MirrorCS")}),1.0]])]});
            var Q3;
            Q3=makeQuery(id+"F1.imprint","IMPRINT",FACE,{"disambiguationData":[TD([[makeQuery(id+"F1.imprint","IMPRINT",EDGE,{"derivedFrom":sQuery(id+"F1.wireOp",EDGE,"E417")}),-1.0]])]});
            var Q4;
            Q4=makeQuery(id+"F0.imprint","IMPRINT",FACE,{"disambiguationData":[TD([[makeQuery(id+"F0.imprint","IMPRINT",EDGE,{"derivedFrom":sQuery(id+"F0.wireOp",EDGE,"E285.MirrorCS")}),-1.0]])]});
            var Q5;
            Q5=makeQuery(id+"F0.imprint","IMPRINT",FACE,{"disambiguationData":[TD([[makeQuery(id+"F0.imprint","IMPRINT",EDGE,{"derivedFrom":sQuery(id+"F0.wireOp",EDGE,"E90")}),1.0]])]});
            var Q6;
            Q6=makeQuery(id+"F0.imprint","IMPRINT",FACE,{"disambiguationData":[TD([[makeQuery(id+"F0.imprint","IMPRINT",EDGE,{"derivedFrom":sQuery(id+"F0.wireOp",EDGE,"E409")}),1.0]])]});
            var Q7;
            Q7=makeQuery(id+"F0.imprint","IMPRINT",FACE,{"disambiguationData":[TD([[makeQuery(id+"F0.imprint","IMPRINT",EDGE,{"derivedFrom":sQuery(id+"F0.wireOp",EDGE,"E413.MirrorC")}),1.0]])]});
            var Q8;
            {var subQ1=sQuery(id+"F0.wireOp",EDGE,"E406");Q8=makeQuery(id+"F0.imprint","IMPRINT",FACE,{"disambiguationData":[TD([[makeQuery(id+"F0.imprint","IMPRINT",EDGE,{"derivedFrom":subQ1}),-1.0]])]});}
            var Q9;
            {var subQ1=sQuery(id+"F0.wireOp",EDGE,"E410.MirrorCS");Q9=makeQuery(id+"F0.imprint","IMPRINT",FACE,{"disambiguationData":[TD([[makeQuery(id+"F0.imprint","IMPRINT",EDGE,{"derivedFrom":subQ1}),-1.0]])]});}
            extrude(context, id + "F4", {"entities" : qUnion([Q0, Q1, Q2, Q3, Q4, Q5, Q6, Q7, Q8, Q9]), "operationType" : NewBodyOperationType.ADD, "oppositeDirection" : true, "depth" : 0.5 * mm});
        }
        {
            var Q0;
            Q0=qCreatedBy(makeId("Front.planeOp"),FACE);
            var sketch = newSketch(context, id + "F5", { "sketchPlane" : qUnion([Q0])});
            skLineSegment(sketch, "E490", {"start": v(7.24, 1.4) * mm, "end": v(-14.45, 1.4) * mm});
            skLineSegment(sketch, "E491", {"start": v(7.24, 2.13) * mm, "end": v(-3.6, 2.13) * mm});
            skLineSegment(sketch, "E492", {"start": v(-3.6, 2.13) * mm, "end": v(-3.6, 17.27) * mm});
            skCircle(sketch, "E493", {"center": v(-3.6, 9.25) * mm, "radius": 0.84 * mm});
            skLineSegment(sketch, "E494", {"start": v(-3.6, 10.75) * mm, "end": v(-18.72, 10.75) * mm});
            skLineSegment(sketch, "E495", {"start": v(-3.6, 10.75) * mm, "end": v(10.88, 10.75) * mm});
            skSolve(sketch);
        }
        {
            var Q0;
            Q0 = qSketchRegion(id + "F5", true);
            extrude(context, id + "F6", {"entities" : qUnion([Q0]), "operationType" : NewBodyOperationType.REMOVE, "depth" : 3 * mm});
        }
    });
